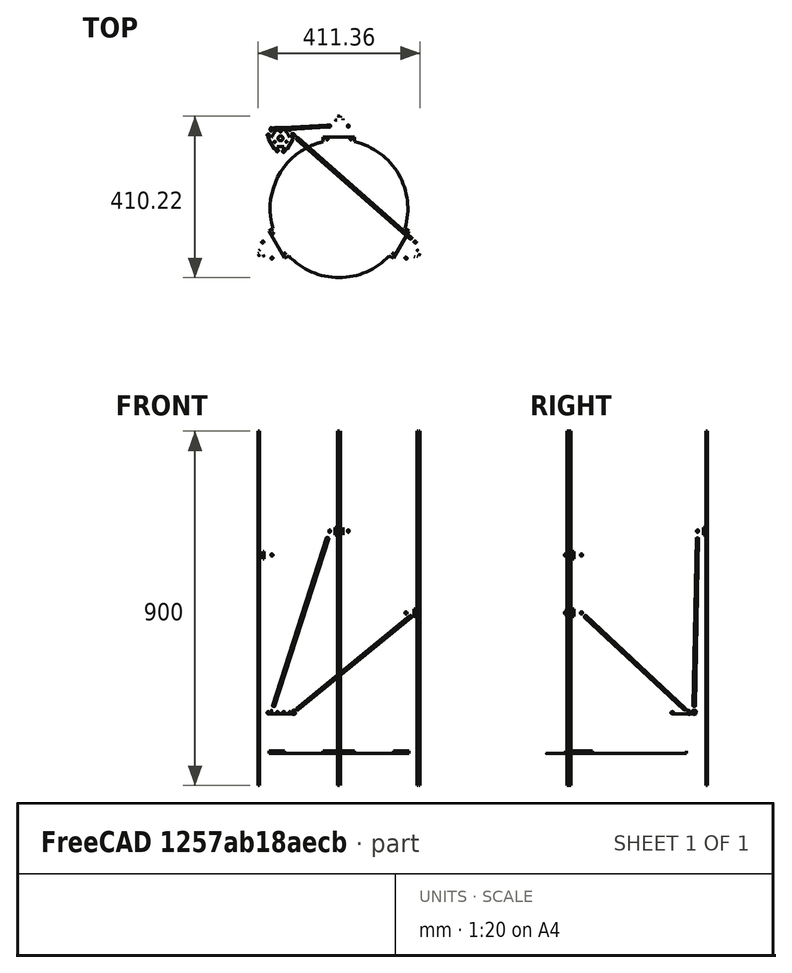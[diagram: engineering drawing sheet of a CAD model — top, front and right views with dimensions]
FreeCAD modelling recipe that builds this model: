
FCSTD DOCUMENT  (FreeCAD 2022.430R26244 +4758 (Git))
Label: AGAsm3MonsterKosselVs
License: All rights reserved
LicenseURL: http://en.wikipedia.org/wiki/All_rights_reserved
objects: App::FeaturePython×78, Part::FeaturePython×52, App::LinkElement×7, App::Link×4
note: 51 computed .brp shape members not serialized (recipe doc carries the construction recipe); baked Part::Feature solids carry a one-line shape summary decoded from their .brp
EXTERNAL_REF file=SubAs3Bati.FCStd obj=Assembly
EXTERNAL_REF file=SubAs3kossel_carriage_MGN9C.FCStd obj=Assembly
EXTERNAL_REF file=As3rod.FCStd obj=Assembly001
EXTERNAL_REF file=As3DeltaEffector.FCStd obj=Assembly002

FEATURE [App::Link] Link  label="SubAs3Bati"
  AutoLinkLabel = false
  AutoPlacement = true
  LinkedObject = -> <external SubAs3Bati.FCStd>#Assembly
  SyncGroupVisibility = false
  TreeRank = 0
  _LinkOwner = 275
  _LinkVersion = 1
FEATURE [App::LinkElement] Link001_i0
  LinkPlacement = pos=(163.421,1.55193e-09,3.43782) rot=(0,0,1;0rad)
  LinkedObject = -> <external SubAs3kossel_carriage_MGN9C.FCStd>#Assembly
  Placement = pos=(163.421,1.55193e-09,3.43782) rot=(0,0,1;0rad)
  TreeRank = 0
  _LinkOwner = 277
  _LinkVersion = 1
FEATURE [App::LinkElement] Link001_i1
  LinkPlacement = pos=(-44.3214,-201.973,353.265) rot=(1,0,0;4.18879rad)
  LinkedObject = -> <external SubAs3kossel_carriage_MGN9C.FCStd>#Assembly
  Placement = pos=(-44.3214,-201.973,353.265) rot=(1,0,0;4.18879rad)
  TreeRank = 0
  _LinkOwner = 277
  _LinkVersion = 1
FEATURE [App::LinkElement] Link001_i2
  LinkPlacement = pos=(16.3978,201.973,353.265) rot=(1,0,0;2.0944rad)
  LinkedObject = -> <external SubAs3kossel_carriage_MGN9C.FCStd>#Assembly
  Placement = pos=(16.3978,201.973,353.265) rot=(1,0,0;2.0944rad)
  TreeRank = 0
  _LinkOwner = 277
  _LinkVersion = 1
FEATURE [App::Link] Link001  label="SubAs3kossel_carriage_MGN9C"
  AutoLinkLabel = false
  AutoPlacement = true
  ElementCount = 3
  ElementList = -> [Link001_i0,Link001_i1,Link001_i2]
  LinkPlacement = pos=(204.95,-118.328,535) rot=(-0.694747,0.186157,0.694747;2.77349rad)
  LinkedObject = -> <external SubAs3kossel_carriage_MGN9C.FCStd>#Assembly
  Placement = pos=(204.95,-118.328,535) rot=(-0.694747,0.186157,0.694747;2.77349rad)
  SyncGroupVisibility = false
  TreeRank = 0
  _LinkOwner = 275
  _LinkVersion = 1
FEATURE [App::LinkElement] Link002_i0
  LinkPlacement = pos=(-35.9157,116.302,169.62) rot=(-0.350458,-0.806618,0.475969;5.10642rad)
  LinkedObject = -> <external As3rod.FCStd>#Assembly001
  Placement = pos=(-35.9157,116.302,169.62) rot=(-0.350458,-0.806618,0.475969;5.10642rad)
  TreeRank = 0
  _LinkOwner = 339
  _LinkVersion = 1
FEATURE [App::LinkElement] Link002_i1
  LinkPlacement = pos=(-133.494,204.013,223.964) rot=(-0.162867,0.145143,-0.975914;1.59805rad)
  LinkedObject = -> <external As3rod.FCStd>#Assembly001
  Placement = pos=(-133.494,204.013,223.964) rot=(-0.162867,0.145143,-0.975914;1.59805rad)
  TreeRank = 0
  _LinkOwner = 339
  _LinkVersion = 1
FEATURE [App::LinkElement] Link002_i2
  LinkPlacement = pos=(-160.329,76.1826,208.178) rot=(-0.107213,-0.289287,0.951219;3.72729rad)
  LinkedObject = -> <external As3rod.FCStd>#Assembly001
  Placement = pos=(-160.329,76.1826,208.178) rot=(-0.107213,-0.289287,0.951219;3.72729rad)
  TreeRank = 0
  _LinkOwner = 339
  _LinkVersion = 1
FEATURE [App::Link] Link003  label="As3DeltaEffector"
  AutoLinkLabel = false
  AutoPlacement = true
  LinkPlacement = pos=(-152.152,159.446,131.794) rot=(0,0,-1;3.66519rad)
  LinkedObject = -> <external As3DeltaEffector.FCStd>#Assembly002
  Placement = pos=(-152.152,159.446,131.794) rot=(0,0,-1;3.66519rad)
  SyncGroupVisibility = false
  TreeRank = 0
  _LinkOwner = 275
  _LinkVersion = 1
FEATURE [App::LinkElement] Link002_i3
  LinkPlacement = pos=(-59.4057,75.6158,169.62) rot=(-0.350454,-0.806617,0.475973;5.10642rad)
  LinkedObject = -> <external As3rod.FCStd>#Assembly001
  Placement = pos=(-59.4057,75.6158,169.62) rot=(-0.350454,-0.806617,0.475973;5.10642rad)
  TreeRank = 0
  _LinkOwner = 339
  _LinkVersion = 1
FEATURE [App::Link] Link002  label="As3Rod"
  AutoLinkLabel = false
  AutoPlacement = true
  ElementCount = 4
  ElementList = -> [Link002_i0,Link002_i1,Link002_i2,Link002_i3]
  LinkedObject = -> <external As3rod.FCStd>#Assembly001
  SyncGroupVisibility = false
  TreeRank = 0
  _LinkOwner = 275
  _LinkVersion = 1
FEATURE [Part::FeaturePython] Parts  # WARN: FeaturePython — macro-defined, semantics opaque (R4)
  Group = -> [Link,Link001,Link003,Link002]
  GroupMode = 0
  TreeRank = 0
  _LinkVersion = 1
FEATURE [Part::FeaturePython] Assembly  label="Asm3MonsterKossel"  # WARN: FeaturePython — macro-defined, semantics opaque (R4)
  AutoRelax = true
  BuildShape = 0
  Freeze = false
  Group = -> [Constraints,Elements,Parts]
  TreeRank = 0
  Verbose = false
  _LinkVersion = 1
  _SolverType = 1
  _Version = 1
FEATURE [App::FeaturePython] Constraints  # WARN: FeaturePython — macro-defined, semantics opaque (R4)
  Group = -> [Constraint,Constraint003,Constraint004,Constraint005,Constraint006,Constraint007,Constraint008,Constraint021,Constraint010,Constraint019,Constraint011,Constraint016,Constraint012,Constraint020,Constraint022,Constraint009,Constraint026,Constraint027,Constraint028,Constraint029,Constraint030,Constraint031,Constraint032,Constraint023,Constraint024,Constraint025]
  TreeRank = 0
  _LinkVersion = 1
  _Version = 1
FEATURE [App::FeaturePython] Elements  # WARN: FeaturePython — macro-defined, semantics opaque (R4)
  Group = -> [_Element,_Element002,_Element003,_Element005,_Element007,_Element008,_Element010,_Element013,_Element014,_Element015,_Element016,_Element017,_Element018,_Element019,_Element020,_Element021,_Element022,_Element023,_Element024,_Element025,_Element026,_Element027,_Element028,_Element030,_Element032,_Element034,_Element035,_Element036,_Element037,_Element038,_Element039,_Element040,_Element041,+17 more]
  TreeRank = 0
  _LinkVersion = 1
FEATURE [Part::FeaturePython] _Element  label="Fix@SubAs3Bati@#0"  # link proxy (typed FeaturePython)
  Detach = false
  LinkTransform = true
  LinkedObject = -> Link [1.$Fix@SubAs3Column@#0.]
  TreeRank = 0
  _LinkVersion = 1
  _Parent = -> Elements
FEATURE [App::FeaturePython] Constraint  label="Locked"  # WARN: FeaturePython — macro-defined, semantics opaque (R4)
  Disabled = false
  Group = -> [ElementLink]
  TreeRank = 0
  _ConstraintType = 0
  _LinkVersion = 1
  _Parent = -> Constraints
FEATURE [App::FeaturePython] ElementLink  label="Fix1@SubAs3Bati@"  # link proxy (typed FeaturePython)
  LinkTransform = true
  LinkedObject = -> _Element002
  TreeRank = 0
  _LinkVersion = 1
  _Parent = -> Constraint
FEATURE [Part::FeaturePython] _Element002  label="Fix1@SubAs3Bati@"  # link proxy (typed FeaturePython)
  Detach = false
  LinkTransform = true
  LinkedObject = -> Link [1.$Fix1@As3bed@.]
  TreeRank = 0
  _LinkVersion = 1
  _Parent = -> Elements
FEATURE [App::FeaturePython] Constraint003  label="PlaneAlignment"  # WARN: FeaturePython — macro-defined, semantics opaque (R4)
  Angle = 0
  AnglePitch = 0
  AngleRoll = 0
  Cascade = false
  Disabled = false
  Group = -> [ElementLink005,ElementLink006]
  LockAngle = false
  Offset = -10
  TreeRank = 0
  _ConstraintType = 37
  _LinkVersion = 1
  _Parent = -> Constraints
FEATURE [App::FeaturePython] ElementLink005  label="Ref@SubAs3Bati@#0"  # link proxy (typed FeaturePython)
  LinkTransform = true
  LinkedObject = -> _Element003
  TreeRank = 0
  _LinkVersion = 1
  _Parent = -> Constraint003
FEATURE [Part::FeaturePython] _Element003  label="Ref@SubAs3Bati@#0"  # link proxy (typed FeaturePython)
  Detach = false
  LinkTransform = true
  LinkedObject = -> Link [1.$Ref@SubAs3Column@#0.]
  TreeRank = 0
  _LinkVersion = 1
  _Parent = -> Elements
FEATURE [App::FeaturePython] ElementLink006  label="Ref@SubAs3kossel_carriage_MGN9C@#0"  # link proxy (typed FeaturePython)
  LinkTransform = true
  LinkedObject = -> _Element014
  TreeRank = 0
  _LinkVersion = 1
  _Parent = -> Constraint003
FEATURE [App::FeaturePython] Constraint004  label="PlaneAlignment001"  # WARN: FeaturePython — macro-defined, semantics opaque (R4)
  Angle = 0
  AnglePitch = 0
  AngleRoll = 0
  Cascade = false
  Disabled = false
  Group = -> [ElementLink007,ElementLink008]
  LockAngle = false
  Offset = -5.5
  TreeRank = 0
  _ConstraintType = 37
  _LinkVersion = 1
  _Parent = -> Constraints
FEATURE [App::FeaturePython] ElementLink007  label="Lat@SubAs3kossel_carriage_MGN9C@#0"  # link proxy (typed FeaturePython)
  LinkTransform = true
  LinkedObject = -> _Element015
  TreeRank = 0
  _LinkVersion = 1
  _Parent = -> Constraint004
FEATURE [App::FeaturePython] ElementLink008  label="Lat@SubAs3Bati@#0"  # link proxy (typed FeaturePython)
  LinkTransform = true
  LinkedObject = -> _Element005
  TreeRank = 0
  _LinkVersion = 1
  _Parent = -> Constraint004
FEATURE [Part::FeaturePython] _Element005  label="Lat@SubAs3Bati@#0"  # link proxy (typed FeaturePython)
  Detach = false
  LinkTransform = true
  LinkedObject = -> Link [1.$Lat@SubAs3Column@#0.]
  TreeRank = 0
  _LinkVersion = 1
  _Parent = -> Elements
FEATURE [App::FeaturePython] Constraint005  label="PlaneAlignment002"  # WARN: FeaturePython — macro-defined, semantics opaque (R4)
  Angle = 0
  AnglePitch = 0
  AngleRoll = 0
  Cascade = false
  Disabled = false
  Group = -> [ElementLink009,ElementLink010]
  LockAngle = false
  Offset = -10
  TreeRank = 0
  _ConstraintType = 37
  _LinkVersion = 1
  _Parent = -> Constraints
FEATURE [App::FeaturePython] ElementLink009  label="Ref@SubAs3kossel_carriage_MGN9C@#1"  # link proxy (typed FeaturePython)
  LinkTransform = true
  LinkedObject = -> _Element016
  TreeRank = 0
  _LinkVersion = 1
  _Parent = -> Constraint005
FEATURE [App::FeaturePython] ElementLink010  label="Ref@SubAs3Bati@#1"  # link proxy (typed FeaturePython)
  LinkTransform = true
  LinkedObject = -> _Element007
  TreeRank = 0
  _LinkVersion = 1
  _Parent = -> Constraint005
FEATURE [Part::FeaturePython] _Element007  label="Ref@SubAs3Bati@#1"  # link proxy (typed FeaturePython)
  Detach = false
  LinkTransform = true
  LinkedObject = -> Link [1.$Ref@SubAs3Column@#1.]
  TreeRank = 0
  _LinkVersion = 1
  _Parent = -> Elements
FEATURE [App::FeaturePython] Constraint006  label="PlaneAlignment003"  # WARN: FeaturePython — macro-defined, semantics opaque (R4)
  Angle = 0
  AnglePitch = 0
  AngleRoll = 0
  Cascade = false
  Disabled = false
  Group = -> [ElementLink011,ElementLink012]
  LockAngle = false
  Offset = 5.5
  TreeRank = 0
  _ConstraintType = 37
  _LinkVersion = 1
  _Parent = -> Constraints
FEATURE [App::FeaturePython] ElementLink011  label="Lat@SubAs3Bati@#1"  # link proxy (typed FeaturePython)
  LinkTransform = true
  LinkedObject = -> _Element008
  TreeRank = 0
  _LinkVersion = 1
  _Parent = -> Constraint006
FEATURE [Part::FeaturePython] _Element008  label="Lat@SubAs3Bati@#1"  # link proxy (typed FeaturePython)
  Detach = false
  LinkTransform = true
  LinkedObject = -> Link [1.$Lat@SubAs3Column@#1.]
  TreeRank = 0
  _LinkVersion = 1
  _Parent = -> Elements
FEATURE [App::FeaturePython] ElementLink012  label="Lat@SubAs3kossel_carriage_MGN9C@#1"  # link proxy (typed FeaturePython)
  LinkTransform = true
  LinkedObject = -> _Element017
  TreeRank = 0
  _LinkVersion = 1
  _Parent = -> Constraint006
FEATURE [App::FeaturePython] Constraint007  label="PlaneAlignment004"  # WARN: FeaturePython — macro-defined, semantics opaque (R4)
  Angle = 0
  AnglePitch = 0
  AngleRoll = 0
  Cascade = false
  Disabled = false
  Group = -> [ElementLink013,ElementLink014]
  LockAngle = false
  Offset = -10
  TreeRank = 0
  _ConstraintType = 37
  _LinkVersion = 1
  _Parent = -> Constraints
FEATURE [App::FeaturePython] ElementLink013  label="Ref@SubAs3Bati@#2"  # link proxy (typed FeaturePython)
  LinkTransform = true
  LinkedObject = -> _Element010
  TreeRank = 0
  _LinkVersion = 1
  _Parent = -> Constraint007
FEATURE [Part::FeaturePython] _Element010  label="Ref@SubAs3Bati@#2"  # link proxy (typed FeaturePython)
  Detach = false
  LinkTransform = true
  LinkedObject = -> Link [1.$Ref@SubAs3Column@#2.]
  TreeRank = 0
  _LinkVersion = 1
  _Parent = -> Elements
FEATURE [App::FeaturePython] ElementLink014  label="Ref@SubAs3kossel_carriage_MGN9C@#2"  # link proxy (typed FeaturePython)
  LinkTransform = true
  LinkedObject = -> _Element018
  TreeRank = 0
  _LinkVersion = 1
  _Parent = -> Constraint007
FEATURE [App::FeaturePython] Constraint008  label="PlaneAlignment005"  # WARN: FeaturePython — macro-defined, semantics opaque (R4)
  Angle = 0
  AnglePitch = 0
  AngleRoll = 0
  Cascade = false
  Disabled = false
  Group = -> [ElementLink015,ElementLink016]
  LockAngle = false
  Offset = -5.5
  TreeRank = 0
  _ConstraintType = 37
  _LinkVersion = 1
  _Parent = -> Constraints
FEATURE [App::FeaturePython] ElementLink015  label="Lat@SubAs3kossel_carriage_MGN9C@#2"  # link proxy (typed FeaturePython)
  LinkTransform = true
  LinkedObject = -> _Element019
  TreeRank = 0
  _LinkVersion = 1
  _Parent = -> Constraint008
FEATURE [App::FeaturePython] ElementLink016  label="Lat@SubAs3Bati@#2"  # link proxy (typed FeaturePython)
  LinkTransform = true
  LinkedObject = -> _Element013
  TreeRank = 0
  _LinkVersion = 1
  _Parent = -> Constraint008
FEATURE [Part::FeaturePython] _Element013  label="Lat@SubAs3Bati@#2"  # link proxy (typed FeaturePython)
  Detach = false
  LinkTransform = true
  LinkedObject = -> Link [1.$Lat@SubAs3Column@#2.]
  TreeRank = 0
  _LinkVersion = 1
  _Parent = -> Elements
FEATURE [Part::FeaturePython] _Element014  label="Ref@SubAs3kossel_carriage_MGN9C@#0"  # link proxy (typed FeaturePython)
  Detach = false
  LinkTransform = true
  LinkedObject = -> Link001 [Link001_i0.1.$Ref@As3MGN9CZFC-HiwinCorporation-3D-10-31-2021@.]
  TreeRank = 0
  _LinkVersion = 1
  _Parent = -> Elements
FEATURE [Part::FeaturePython] _Element015  label="Lat@SubAs3kossel_carriage_MGN9C@#0"  # link proxy (typed FeaturePython)
  Detach = false
  LinkTransform = true
  LinkedObject = -> Link001 [Link001_i0.1.$Lat@As3MGN9CZFC-HiwinCorporation-3D-10-31-2021@.]
  TreeRank = 0
  _LinkVersion = 1
  _Parent = -> Elements
FEATURE [Part::FeaturePython] _Element016  label="Ref@SubAs3kossel_carriage_MGN9C@#1"  # link proxy (typed FeaturePython)
  Detach = false
  LinkTransform = true
  LinkedObject = -> Link001 [Link001_i1.1.$Ref@As3MGN9CZFC-HiwinCorporation-3D-10-31-2021@.]
  TreeRank = 0
  _LinkVersion = 1
  _Parent = -> Elements
FEATURE [Part::FeaturePython] _Element017  label="Lat@SubAs3kossel_carriage_MGN9C@#1"  # link proxy (typed FeaturePython)
  Detach = false
  LinkTransform = true
  LinkedObject = -> Link001 [Link001_i1.1.$Lat@As3MGN9CZFC-HiwinCorporation-3D-10-31-2021@.]
  TreeRank = 0
  _LinkVersion = 1
  _Parent = -> Elements
FEATURE [Part::FeaturePython] _Element018  label="Ref@SubAs3kossel_carriage_MGN9C@#2"  # link proxy (typed FeaturePython)
  Detach = false
  LinkTransform = true
  LinkedObject = -> Link001 [Link001_i2.1.$Ref@As3MGN9CZFC-HiwinCorporation-3D-10-31-2021@.]
  TreeRank = 0
  _LinkVersion = 1
  _Parent = -> Elements
FEATURE [Part::FeaturePython] _Element019  label="Lat@SubAs3kossel_carriage_MGN9C@#2"  # link proxy (typed FeaturePython)
  Detach = false
  LinkTransform = true
  LinkedObject = -> Link001 [Link001_i2.1.$Lat@As3MGN9CZFC-HiwinCorporation-3D-10-31-2021@.]
  TreeRank = 0
  _LinkVersion = 1
  _Parent = -> Elements
FEATURE [App::FeaturePython] Constraint009  label="PlaneAlignment006"  # WARN: FeaturePython — macro-defined, semantics opaque (R4)
  Angle = 0
  AnglePitch = 0
  AngleRoll = 0
  Cascade = false
  Disabled = false
  Group = -> [ElementLink017,ElementLink018]
  LockAngle = false
  Offset = 100
  TreeRank = 0
  _ConstraintType = 37
  _LinkVersion = 1
  _Parent = -> Constraints
FEATURE [App::FeaturePython] ElementLink017  label="Element001@As3DeltaEffector@"  # link proxy (typed FeaturePython)
  LinkTransform = true
  LinkedObject = -> _Element020
  TreeRank = 0
  _LinkVersion = 1
  _Parent = -> Constraint009
FEATURE [Part::FeaturePython] _Element020  label="Element001@As3DeltaEffector@"  # link proxy (typed FeaturePython)
  Detach = false
  LinkTransform = true
  LinkedObject = -> Link003 [1.$Element001.]
  TreeRank = 0
  _LinkVersion = 1
  _Parent = -> Elements
FEATURE [App::FeaturePython] ElementLink018  label="_Element021"  # link proxy (typed FeaturePython)
  LinkTransform = true
  LinkedObject = -> _Element021
  TreeRank = 0
  _LinkVersion = 1
  _Parent = -> Constraint009
FEATURE [Part::FeaturePython] _Element021  # link proxy (typed FeaturePython)
  Detach = false
  LinkTransform = true
  LinkedObject = -> Link [1.$Element007.]
  TreeRank = 0
  _LinkVersion = 1
  _Parent = -> Elements
FEATURE [App::FeaturePython] Constraint010  label="PointsCoincident"  # WARN: FeaturePython — macro-defined, semantics opaque (R4)
  Disabled = false
  Group = -> [ElementLink019,ElementLink020]
  TreeRank = 0
  _ConstraintType = 1
  _LinkVersion = 1
  _Parent = -> Constraints
FEATURE [App::FeaturePython] ElementLink019  label="ElSphereF@As3Rod@#0#0"  # link proxy (typed FeaturePython)
  LinkTransform = true
  LinkedObject = -> _Element022
  TreeRank = 0
  _LinkVersion = 1
  _Parent = -> Constraint010
FEATURE [Part::FeaturePython] _Element022  label="ElSphereF@As3Rod@#0#0"  # link proxy (typed FeaturePython)
  Detach = false
  LinkTransform = true
  LinkedObject = -> Link002 [Link002_i0.1.$ElSphereF@As3rodEnd5347@#0.]
  TreeRank = 0
  _LinkVersion = 1
  _Parent = -> Elements
FEATURE [App::FeaturePython] ElementLink020  label="ElSphereM@As3DeltaEffector@#0"  # link proxy (typed FeaturePython)
  LinkTransform = true
  LinkedObject = -> _Element023
  TreeRank = 0
  _LinkVersion = 1
  _Parent = -> Constraint010
FEATURE [Part::FeaturePython] _Element023  label="ElSphereM@As3DeltaEffector@#0"  # link proxy (typed FeaturePython)
  Detach = false
  LinkTransform = true
  LinkedObject = -> Link003 [1.$ElSphereM@As3Traxxas5347ball@#0.]
  TreeRank = 0
  _LinkVersion = 1
  _Parent = -> Elements
FEATURE [App::FeaturePython] Constraint011  label="PointsCoincident009"  # WARN: FeaturePython — macro-defined, semantics opaque (R4)
  Disabled = false
  Group = -> [ElementLink021,ElementLink022]
  TreeRank = 0
  _ConstraintType = 1
  _LinkVersion = 1
  _Parent = -> Constraints
FEATURE [App::FeaturePython] ElementLink021  label="ElSphereM@As3DeltaEffector@#4"  # link proxy (typed FeaturePython)
  LinkTransform = true
  LinkedObject = -> _Element030
  TreeRank = 0
  _LinkVersion = 1
  _Parent = -> Constraint011
FEATURE [Part::FeaturePython] _Element024  label="ElSphereM@As3DeltaEffector@#1"  # link proxy (typed FeaturePython)
  Detach = false
  LinkTransform = true
  LinkedObject = -> Link003 [1.$ElSphereM@As3Traxxas5347ball@#1.]
  TreeRank = 0
  _LinkVersion = 1
  _Parent = -> Elements
FEATURE [App::FeaturePython] ElementLink022  label="ElSphereF@As3Rod@#0#1"  # link proxy (typed FeaturePython)
  LinkTransform = true
  LinkedObject = -> _Element025
  TreeRank = 0
  _LinkVersion = 1
  _Parent = -> Constraint011
FEATURE [Part::FeaturePython] _Element025  label="ElSphereF@As3Rod@#0#1"  # link proxy (typed FeaturePython)
  Detach = false
  LinkTransform = true
  LinkedObject = -> Link002 [Link002_i1.1.$ElSphereF@As3rodEnd5347@#0.]
  TreeRank = 0
  _LinkVersion = 1
  _Parent = -> Elements
FEATURE [App::FeaturePython] Constraint012  label="PointsCoincident010"  # WARN: FeaturePython — macro-defined, semantics opaque (R4)
  Disabled = false
  Group = -> [ElementLink023,ElementLink024]
  TreeRank = 0
  _ConstraintType = 1
  _LinkVersion = 1
  _Parent = -> Constraints
FEATURE [App::FeaturePython] ElementLink023  label="ElSphereM@As3DeltaEffector@#2"  # link proxy (typed FeaturePython)
  LinkTransform = true
  LinkedObject = -> _Element026
  TreeRank = 0
  _LinkVersion = 1
  _Parent = -> Constraint012
FEATURE [Part::FeaturePython] _Element026  label="ElSphereM@As3DeltaEffector@#2"  # link proxy (typed FeaturePython)
  Detach = false
  LinkTransform = true
  LinkedObject = -> Link003 [1.$ElSphereM@As3Traxxas5347ball@#2.]
  TreeRank = 0
  _LinkVersion = 1
  _Parent = -> Elements
FEATURE [App::FeaturePython] ElementLink024  label="ElSphereF@As3Rod@#0#2"  # link proxy (typed FeaturePython)
  LinkTransform = true
  LinkedObject = -> _Element027
  TreeRank = 0
  _LinkVersion = 1
  _Parent = -> Constraint012
FEATURE [Part::FeaturePython] _Element027  label="ElSphereF@As3Rod@#0#2"  # link proxy (typed FeaturePython)
  Detach = false
  LinkTransform = true
  LinkedObject = -> Link002 [Link002_i2.1.$ElSphereF@As3rodEnd5347@#0.]
  TreeRank = 0
  _LinkVersion = 1
  _Parent = -> Elements
FEATURE [Part::FeaturePython] _Element028  label="ElSphereM@As3DeltaEffector@#3"  # link proxy (typed FeaturePython)
  Detach = false
  LinkTransform = true
  LinkedObject = -> Link003 [1.$ElSphereM@As3Traxxas5347ball@#3.]
  TreeRank = 0
  _LinkVersion = 1
  _Parent = -> Elements
FEATURE [Part::FeaturePython] _Element030  label="ElSphereM@As3DeltaEffector@#4"  # link proxy (typed FeaturePython)
  Detach = false
  LinkTransform = true
  LinkedObject = -> Link003 [1.$ElSphereM@As3Traxxas5347ball@#4.]
  TreeRank = 0
  _LinkVersion = 1
  _Parent = -> Elements
FEATURE [Part::FeaturePython] _Element032  label="ElSphereM@As3DeltaEffector@#5"  # link proxy (typed FeaturePython)
  Detach = false
  LinkTransform = true
  LinkedObject = -> Link003 [1.$ElSphereM@As3Traxxas5347ball@#5.]
  TreeRank = 0
  _LinkVersion = 1
  _Parent = -> Elements
FEATURE [App::FeaturePython] Constraint016  label="PointsCoincident014"  # WARN: FeaturePython — macro-defined, semantics opaque (R4)
  Disabled = false
  Group = -> [ElementLink031,ElementLink032]
  TreeRank = 0
  _ConstraintType = 1
  _LinkVersion = 1
  _Parent = -> Constraints
FEATURE [App::FeaturePython] ElementLink031  label="ElSphereM@SubAs3kossel_carriage_MGN9C@#1#1"  # link proxy (typed FeaturePython)
  LinkTransform = true
  LinkedObject = -> _Element050
  TreeRank = 0
  _LinkVersion = 1
  _Parent = -> Constraint016
FEATURE [Part::FeaturePython] _Element034  label="ElSphereM@SubAs3kossel_carriage_MGN9C@#0#0"  # link proxy (typed FeaturePython)
  Detach = false
  LinkTransform = true
  LinkedObject = -> Link001 [Link001_i0.1.$ElSphereM@As3Traxxas5347ball@#0.]
  TreeRank = 0
  _LinkVersion = 1
  _Parent = -> Elements
FEATURE [App::FeaturePython] ElementLink032  label="ElSphereF@As3Rod@#1#1"  # link proxy (typed FeaturePython)
  LinkTransform = true
  LinkedObject = -> _Element035
  TreeRank = 0
  _LinkVersion = 1
  _Parent = -> Constraint016
FEATURE [Part::FeaturePython] _Element035  label="ElSphereF@As3Rod@#1#1"  # link proxy (typed FeaturePython)
  Detach = false
  LinkTransform = true
  LinkedObject = -> Link002 [Link002_i1.1.$ElSphereF@As3rodEnd5347@#1.]
  TreeRank = 0
  _LinkVersion = 1
  _Parent = -> Elements
FEATURE [Part::FeaturePython] _Element036  # link proxy (typed FeaturePython)
  Detach = false
  LinkTransform = true
  LinkedObject = -> Link002 [1.1.$Element004.]
  TreeRank = 0
  _LinkVersion = 1
  _Parent = -> Elements
FEATURE [Part::FeaturePython] _Element037  # link proxy (typed FeaturePython)
  Detach = false
  LinkTransform = true
  LinkedObject = -> Link003 [1.$Element011.]
  TreeRank = 0
  _LinkVersion = 1
  _Parent = -> Elements
FEATURE [Part::FeaturePython] _Element038  # link proxy (typed FeaturePython)
  Detach = false
  LinkTransform = true
  LinkedObject = -> Link003 [1.$Element012.]
  TreeRank = 0
  _LinkVersion = 1
  _Parent = -> Elements
FEATURE [Part::FeaturePython] _Element039  label="ElPlane@As3Rod@#001#0"  # link proxy (typed FeaturePython)
  Detach = false
  LinkTransform = true
  LinkedObject = -> Link002 [0.1.$ElPlane@As3rodEnd5347@#001.]
  TreeRank = 0
  _LinkVersion = 1
  _Parent = -> Elements
FEATURE [App::FeaturePython] Constraint019  label="PointsCoincident015"  # WARN: FeaturePython — macro-defined, semantics opaque (R4)
  Disabled = false
  Group = -> [ElementLink037,ElementLink038]
  TreeRank = 0
  _ConstraintType = 1
  _LinkVersion = 1
  _Parent = -> Constraints
FEATURE [App::FeaturePython] ElementLink037  label="ElSphereM@SubAs3kossel_carriage_MGN9C@#1#0"  # link proxy (typed FeaturePython)
  LinkTransform = true
  LinkedObject = -> _Element040
  TreeRank = 0
  _LinkVersion = 1
  _Parent = -> Constraint019
FEATURE [Part::FeaturePython] _Element040  label="ElSphereM@SubAs3kossel_carriage_MGN9C@#1#0"  # link proxy (typed FeaturePython)
  Detach = false
  LinkTransform = true
  LinkedObject = -> Link001 [Link001_i0.1.$ElSphereM@As3Traxxas5347ball@#1.]
  TreeRank = 0
  _LinkVersion = 1
  _Parent = -> Elements
FEATURE [App::FeaturePython] ElementLink038  label="ElSphereF@As3Rod@#1#0"  # link proxy (typed FeaturePython)
  LinkTransform = true
  LinkedObject = -> _Element041
  TreeRank = 0
  _LinkVersion = 1
  _Parent = -> Constraint019
FEATURE [Part::FeaturePython] _Element041  label="ElSphereF@As3Rod@#1#0"  # link proxy (typed FeaturePython)
  Detach = false
  LinkTransform = true
  LinkedObject = -> Link002 [Link002_i0.1.$ElSphereF@As3rodEnd5347@#1.]
  TreeRank = 0
  _LinkVersion = 1
  _Parent = -> Elements
FEATURE [App::FeaturePython] Constraint020  label="PointsCoincident008"  # WARN: FeaturePython — macro-defined, semantics opaque (R4)
  Disabled = false
  Group = -> [ElementLink039,ElementLink040]
  TreeRank = 0
  _ConstraintType = 1
  _LinkVersion = 1
  _Parent = -> Constraints
FEATURE [App::FeaturePython] ElementLink039  label="ElSphereM@SubAs3kossel_carriage_MGN9C@#1#2"  # link proxy (typed FeaturePython)
  LinkTransform = true
  LinkedObject = -> _Element042
  TreeRank = 0
  _LinkVersion = 1
  _Parent = -> Constraint020
FEATURE [Part::FeaturePython] _Element042  label="ElSphereM@SubAs3kossel_carriage_MGN9C@#1#2"  # link proxy (typed FeaturePython)
  Detach = false
  LinkTransform = true
  LinkedObject = -> Link001 [Link001_i2.1.$ElSphereM@As3Traxxas5347ball@#1.]
  TreeRank = 0
  _LinkVersion = 1
  _Parent = -> Elements
FEATURE [App::FeaturePython] ElementLink040  label="ElSphereF@As3Rod@#1#2"  # link proxy (typed FeaturePython)
  LinkTransform = true
  LinkedObject = -> _Element043
  TreeRank = 0
  _LinkVersion = 1
  _Parent = -> Constraint020
FEATURE [Part::FeaturePython] _Element043  label="ElSphereF@As3Rod@#1#2"  # link proxy (typed FeaturePython)
  Detach = false
  LinkTransform = true
  LinkedObject = -> Link002 [Link002_i2.1.$ElSphereF@As3rodEnd5347@#1.]
  TreeRank = 0
  _LinkVersion = 1
  _Parent = -> Elements
FEATURE [App::FeaturePython] Constraint021  label="Locked001"  # WARN: FeaturePython — macro-defined, semantics opaque (R4)
  Disabled = true
  Group = -> [ElementLink041]
  TreeRank = 0
  _ConstraintType = 0
  _LinkVersion = 1
  _Parent = -> Constraints
FEATURE [App::FeaturePython] ElementLink041  label="Element001@As3DeltaEffector@"  # link proxy (typed FeaturePython)
  LinkTransform = true
  LinkedObject = -> _Element020
  TreeRank = 0
  _LinkVersion = 1
  _Parent = -> Constraint021
FEATURE [Part::FeaturePython] _Element044  # link proxy (typed FeaturePython)
  Detach = false
  LinkTransform = true
  LinkedObject = -> Link002 [0.1.$Element007.]
  TreeRank = 0
  _LinkVersion = 1
  _Parent = -> Elements
FEATURE [Part::FeaturePython] _Element045  # link proxy (typed FeaturePython)
  Detach = false
  LinkTransform = true
  LinkedObject = -> Link002 [1.1.$Element007.]
  TreeRank = 0
  _LinkVersion = 1
  _Parent = -> Elements
FEATURE [Part::FeaturePython] _Element046  label="ElSphereM@SubAs3kossel_carriage_MGN9C@#0#2"  # link proxy (typed FeaturePython)
  Detach = false
  LinkTransform = true
  LinkedObject = -> Link001 [Link001_i2.1.$ElSphereM@As3Traxxas5347ball@#0.]
  TreeRank = 0
  _LinkVersion = 1
  _Parent = -> Elements
FEATURE [Part::FeaturePython] _Element048  label="ElSphereM@SubAs3kossel_carriage_MGN9C@#0#1"  # link proxy (typed FeaturePython)
  Detach = false
  LinkTransform = true
  LinkedObject = -> Link001 [Link001_i1.1.$ElSphereM@As3Traxxas5347ball@#0.]
  TreeRank = 0
  _LinkVersion = 1
  _Parent = -> Elements
FEATURE [Part::FeaturePython] _Element050  label="ElSphereM@SubAs3kossel_carriage_MGN9C@#1#1"  # link proxy (typed FeaturePython)
  Detach = false
  LinkTransform = true
  LinkedObject = -> Link001 [Link001_i1.1.$ElSphereM@As3Traxxas5347ball@#1.]
  TreeRank = 0
  _LinkVersion = 1
  _Parent = -> Elements
FEATURE [App::FeaturePython] Constraint022  label="PointsPlaneDistance"  # WARN: FeaturePython — macro-defined, semantics opaque (R4)
  Disabled = true
  Distance = 100
  Group = -> [ElementLink042,ElementLink043]
  TreeRank = 0
  _ConstraintType = 7
  _LinkVersion = 1
  _Parent = -> Constraints
FEATURE [App::FeaturePython] ElementLink042  label="_Element051"  # link proxy (typed FeaturePython)
  LinkTransform = true
  LinkedObject = -> _Element051
  TreeRank = 0
  _LinkVersion = 1
  _Parent = -> Constraint022
FEATURE [Part::FeaturePython] _Element051  # link proxy (typed FeaturePython)
  Detach = false
  LinkTransform = true
  LinkedObject = -> Link003 [1.$Element013.]
  TreeRank = 0
  _LinkVersion = 1
  _Parent = -> Elements
FEATURE [App::FeaturePython] ElementLink043  label="_Element021"  # link proxy (typed FeaturePython)
  LinkTransform = true
  LinkedObject = -> _Element021
  TreeRank = 0
  _LinkVersion = 1
  _Parent = -> Constraint022
FEATURE [App::FeaturePython] Constraint023  label="PointsPlaneDistance001"  # WARN: FeaturePython — macro-defined, semantics opaque (R4)
  Disabled = true
  Distance = -190
  Group = -> [ElementLink044,ElementLink045]
  TreeRank = 0
  _ConstraintType = 7
  _LinkVersion = 1
  _Parent = -> Constraints
FEATURE [App::FeaturePython] ElementLink044  label="_Element051"  # link proxy (typed FeaturePython)
  LinkTransform = true
  LinkedObject = -> _Element051
  TreeRank = 0
  _LinkVersion = 1
  _Parent = -> Constraint023
FEATURE [App::FeaturePython] ElementLink045  label="_Element052"  # link proxy (typed FeaturePython)
  LinkTransform = true
  LinkedObject = -> _Element052
  TreeRank = 0
  _LinkVersion = 1
  _Parent = -> Constraint023
FEATURE [Part::FeaturePython] _Element052  # link proxy (typed FeaturePython)
  Detach = false
  LinkTransform = true
  LinkedObject = -> Link [1.$Element008.]
  TreeRank = 0
  _LinkVersion = 1
  _Parent = -> Elements
FEATURE [App::FeaturePython] Constraint024  label="PointsPlaneDistance002"  # WARN: FeaturePython — macro-defined, semantics opaque (R4)
  Disabled = true
  Distance = -175
  Group = -> [ElementLink046,ElementLink047]
  TreeRank = 0
  _ConstraintType = 7
  _LinkVersion = 1
  _Parent = -> Constraints
FEATURE [App::FeaturePython] ElementLink046  label="_Element051"  # link proxy (typed FeaturePython)
  LinkTransform = true
  LinkedObject = -> _Element051
  TreeRank = 0
  _LinkVersion = 1
  _Parent = -> Constraint024
FEATURE [App::FeaturePython] ElementLink047  label="_Element053"  # link proxy (typed FeaturePython)
  LinkTransform = true
  LinkedObject = -> _Element053
  TreeRank = 0
  _LinkVersion = 1
  _Parent = -> Constraint024
FEATURE [Part::FeaturePython] _Element053  # link proxy (typed FeaturePython)
  Detach = false
  LinkTransform = true
  LinkedObject = -> Link [1.$Element009.]
  TreeRank = 0
  _LinkVersion = 1
  _Parent = -> Elements
FEATURE [App::FeaturePython] Constraint025  label="PointsPlaneDistance003"  # WARN: FeaturePython — macro-defined, semantics opaque (R4)
  Disabled = true
  Distance = -181.17
  Group = -> [ElementLink048,ElementLink049]
  TreeRank = 0
  _ConstraintType = 7
  _LinkVersion = 1
  _Parent = -> Constraints
FEATURE [App::FeaturePython] ElementLink048  label="_Element051"  # link proxy (typed FeaturePython)
  LinkTransform = true
  LinkedObject = -> _Element051
  TreeRank = 0
  _LinkVersion = 1
  _Parent = -> Constraint025
FEATURE [App::FeaturePython] ElementLink049  label="_Element054"  # link proxy (typed FeaturePython)
  LinkTransform = true
  LinkedObject = -> _Element054
  TreeRank = 0
  _LinkVersion = 1
  _Parent = -> Constraint025
FEATURE [Part::FeaturePython] _Element054  # link proxy (typed FeaturePython)
  Detach = false
  LinkTransform = true
  LinkedObject = -> Link [1.$Element010.]
  TreeRank = 0
  _LinkVersion = 1
  _Parent = -> Elements
FEATURE [App::FeaturePython] Constraint026  label="PointsCoincident016"  # WARN: FeaturePython — macro-defined, semantics opaque (R4)
  Disabled = false
  Group = -> [ElementLink050,ElementLink051]
  TreeRank = 0
  _ConstraintType = 1
  _LinkVersion = 1
  _Parent = -> Constraints
FEATURE [App::FeaturePython] ElementLink050  label="ElSphereM@As3DeltaEffector@#1"  # link proxy (typed FeaturePython)
  LinkTransform = true
  LinkedObject = -> _Element024
  TreeRank = 0
  _LinkVersion = 1
  _Parent = -> Constraint026
FEATURE [App::FeaturePython] ElementLink051  label="ElSphereF@As3Rod@#0#3"  # link proxy (typed FeaturePython)
  LinkTransform = true
  LinkedObject = -> _Element055
  TreeRank = 0
  _LinkVersion = 1
  _Parent = -> Constraint026
FEATURE [Part::FeaturePython] _Element055  label="ElSphereF@As3Rod@#0#3"  # link proxy (typed FeaturePython)
  Detach = false
  LinkTransform = true
  LinkedObject = -> Link002 [Link002_i3.1.$ElSphereF@As3rodEnd5347@#0.]
  TreeRank = 0
  _LinkVersion = 1
  _Parent = -> Elements
FEATURE [App::FeaturePython] Constraint027  label="PointsDistance"  # WARN: FeaturePython — macro-defined, semantics opaque (R4)
  Cascade = false
  Disabled = true
  Distance = 0.44
  Group = -> [ElementLink052,ElementLink053]
  TreeRank = 0
  _ConstraintType = 44
  _LinkVersion = 1
  _Parent = -> Constraints
FEATURE [App::FeaturePython] ElementLink052  label="ElSphereM@SubAs3kossel_carriage_MGN9C@#0#0"  # link proxy (typed FeaturePython)
  LinkTransform = true
  LinkedObject = -> _Element034
  TreeRank = 0
  _LinkVersion = 1
  _Parent = -> Constraint027
FEATURE [App::FeaturePython] ElementLink053  label="ElSphereF@As3Rod@#1#3"  # link proxy (typed FeaturePython)
  LinkTransform = true
  LinkedObject = -> _Element056
  TreeRank = 0
  _LinkVersion = 1
  _Parent = -> Constraint027
FEATURE [Part::FeaturePython] _Element056  label="ElSphereF@As3Rod@#1#3"  # link proxy (typed FeaturePython)
  Detach = false
  LinkTransform = true
  LinkedObject = -> Link002 [Link002_i3.1.$ElSphereF@As3rodEnd5347@#1.]
  TreeRank = 0
  _LinkVersion = 1
  _Parent = -> Elements
FEATURE [App::FeaturePython] Constraint028  label="PointsCoincident017"  # WARN: FeaturePython — macro-defined, semantics opaque (R4)
  Disabled = false
  Group = -> [ElementLink054,ElementLink055]
  TreeRank = 0
  _ConstraintType = 1
  _LinkVersion = 1
  _Parent = -> Constraints
FEATURE [App::FeaturePython] ElementLink054  label="ElSphereM@SubAs3kossel_carriage_MGN9C@#0#0"  # link proxy (typed FeaturePython)
  LinkTransform = true
  LinkedObject = -> _Element034
  TreeRank = 0
  _LinkVersion = 1
  _Parent = -> Constraint028
FEATURE [App::FeaturePython] ElementLink055  label="ElSphereF@As3Rod@#1#3"  # link proxy (typed FeaturePython)
  LinkTransform = true
  LinkedObject = -> _Element056
  TreeRank = 0
  _LinkVersion = 1
  _Parent = -> Constraint028
FEATURE [App::FeaturePython] Constraint029  label="PointInPlane"  # WARN: FeaturePython — macro-defined, semantics opaque (R4)
  Disabled = false
  Group = -> [ElementLink056,ElementLink057]
  TreeRank = 0
  _ConstraintType = 3
  _LinkVersion = 1
  _Parent = -> Constraints
FEATURE [App::FeaturePython] ElementLink056  label="ElSphereM@As3DeltaEffector@#1"  # link proxy (typed FeaturePython)
  LinkTransform = true
  LinkedObject = -> _Element024
  TreeRank = 0
  _LinkVersion = 1
  _Parent = -> Constraint029
FEATURE [App::FeaturePython] ElementLink057  label="ElSymSphF@As3Rod@#0#0"  # link proxy (typed FeaturePython)
  LinkTransform = true
  LinkedObject = -> _Element057
  TreeRank = 0
  _LinkVersion = 1
  _Parent = -> Constraint029
FEATURE [Part::FeaturePython] _Element057  label="ElSymSphF@As3Rod@#0#0"  # link proxy (typed FeaturePython)
  Detach = false
  LinkTransform = true
  LinkedObject = -> Link002 [Link002_i0.1.$ElSymSphF@As3rodEnd5347@#0.]
  TreeRank = 0
  _LinkVersion = 1
  _Parent = -> Elements
FEATURE [App::FeaturePython] Constraint030  label="PointInPlane001"  # WARN: FeaturePython — macro-defined, semantics opaque (R4)
  Disabled = false
  Group = -> [ElementLink058,ElementLink059]
  TreeRank = 0
  _ConstraintType = 3
  _LinkVersion = 1
  _Parent = -> Constraints
FEATURE [App::FeaturePython] ElementLink058  label="ElSphereM@As3DeltaEffector@#0"  # link proxy (typed FeaturePython)
  LinkTransform = true
  LinkedObject = -> _Element023
  TreeRank = 0
  _LinkVersion = 1
  _Parent = -> Constraint030
FEATURE [App::FeaturePython] ElementLink059  label="ElSymSphF@As3Rod@#0#3"  # link proxy (typed FeaturePython)
  LinkTransform = true
  LinkedObject = -> _Element058
  TreeRank = 0
  _LinkVersion = 1
  _Parent = -> Constraint030
FEATURE [Part::FeaturePython] _Element058  label="ElSymSphF@As3Rod@#0#3"  # link proxy (typed FeaturePython)
  Detach = false
  LinkTransform = true
  LinkedObject = -> Link002 [Link002_i3.1.$ElSymSphF@As3rodEnd5347@#0.]
  TreeRank = 0
  _LinkVersion = 1
  _Parent = -> Elements
FEATURE [App::FeaturePython] Constraint031  label="PointInPlane002"  # WARN: FeaturePython — macro-defined, semantics opaque (R4)
  Disabled = false
  Group = -> [ElementLink060,ElementLink061]
  TreeRank = 0
  _ConstraintType = 3
  _LinkVersion = 1
  _Parent = -> Constraints
FEATURE [App::FeaturePython] ElementLink060  label="ElSphereM@As3DeltaEffector@#3"  # link proxy (typed FeaturePython)
  LinkTransform = true
  LinkedObject = -> _Element028
  TreeRank = 0
  _LinkVersion = 1
  _Parent = -> Constraint031
FEATURE [App::FeaturePython] ElementLink061  label="ElSymSphF@As3Rod@#0#2"  # link proxy (typed FeaturePython)
  LinkTransform = true
  LinkedObject = -> _Element059
  TreeRank = 0
  _LinkVersion = 1
  _Parent = -> Constraint031
FEATURE [Part::FeaturePython] _Element059  label="ElSymSphF@As3Rod@#0#2"  # link proxy (typed FeaturePython)
  Detach = false
  LinkTransform = true
  LinkedObject = -> Link002 [Link002_i2.1.$ElSymSphF@As3rodEnd5347@#0.]
  TreeRank = 0
  _LinkVersion = 1
  _Parent = -> Elements
FEATURE [App::FeaturePython] Constraint032  label="PointInPlane003"  # WARN: FeaturePython — macro-defined, semantics opaque (R4)
  Disabled = false
  Group = -> [ElementLink062,ElementLink063]
  TreeRank = 0
  _ConstraintType = 3
  _LinkVersion = 1
  _Parent = -> Constraints
FEATURE [App::FeaturePython] ElementLink062  label="ElSphereM@As3DeltaEffector@#5"  # link proxy (typed FeaturePython)
  LinkTransform = true
  LinkedObject = -> _Element032
  TreeRank = 0
  _LinkVersion = 1
  _Parent = -> Constraint032
FEATURE [App::FeaturePython] ElementLink063  label="ElSymSphF@As3Rod@#0#1"  # link proxy (typed FeaturePython)
  LinkTransform = true
  LinkedObject = -> _Element060
  TreeRank = 0
  _LinkVersion = 1
  _Parent = -> Constraint032
FEATURE [Part::FeaturePython] _Element060  label="ElSymSphF@As3Rod@#0#1"  # link proxy (typed FeaturePython)
  Detach = false
  LinkTransform = true
  LinkedObject = -> Link002 [Link002_i1.1.$ElSymSphF@As3rodEnd5347@#0.]
  TreeRank = 0
  _LinkVersion = 1
  _Parent = -> Elements

RESOLVED EXTERNAL PARTS (link-assembly join: the EXTERNAL_REF files above that resolve inside this repo's crawl, each included once):
---- part As3DeltaEffector.FCStd = doc fcstd_bb46bd2530a1 ----
FCSTD DOCUMENT  (FreeCAD 2022.430R26244 +4758 (Git))
Label: As3DeltaEffector
License: All rights reserved
LicenseURL: http://en.wikipedia.org/wiki/All_rights_reserved
objects: Part::FeaturePython×30, App::FeaturePython×27, Part::Feature×9, App::LinkElement×6, App::Part×3, App::Link×2
note: 37 computed .brp shape members not serialized (recipe doc carries the construction recipe); baked Part::Feature solids carry a one-line shape summary decoded from their .brp
EXTERNAL_REF file=As3Traxxas5347BallJoint.FCStd obj=Assembly

FEATURE [App::FeaturePython] Constraints001  # WARN: FeaturePython — macro-defined, semantics opaque (R4)
  TreeRank = 258
  _LinkVersion = 1
  _Version = 1
FEATURE [Part::Feature] Solid  label="e3d nozzle (0.4)"
  Placement = pos=(0,-4.25,4e-16) rot=(0,0,1;0rad)
  TreeRank = 195
  shape: bbox 8.083 x 12.5 x 7 mm, 31 faces (baked)
FEATURE [Part::Feature] Solid001  label="e3d heaterblock"
  Placement = pos=(-5.5,-1.25,6.9e-15) rot=(0,0,1;0rad)
  TreeRank = 196
  shape: bbox 20 x 11.5 x 16 mm, 45 faces (baked)
FEATURE [Part::Feature] Solid002  label="e3d heat break"
  Placement = pos=(0,5.25,4e-16) rot=(0,0,1;0rad)
  TreeRank = 197
  shape: bbox 7 x 21.9 x 7 mm, 23 faces (baked)
FEATURE [Part::Feature] Solid003  label="e3d heatsink"
  Placement = pos=(0,12.35,4e-16) rot=(0,1,0;0.209118rad)
  TreeRank = 198
  shape: bbox 22.3 x 42.7 x 22.3 mm, 92 faces (baked)
FEATURE [Part::Feature] Solid004  label="fan duct"
  Placement = pos=(6.82793,2.62156,26.4875) rot=(0,0,1;0rad)
  TreeRank = 199
  shape: bbox 55.54 x 30 x 38.08 mm, 106 faces (baked)
FEATURE [Part::Feature] Solid005  label="fan sub1"
  Placement = pos=(-0.402046,15.9429,23.9537) rot=(0,0,1;0rad)
  TreeRank = 200
  shape: bbox 30 x 30 x 10 mm, 57 faces (baked)
FEATURE [Part::Feature] Solid006  label="fan sub2"
  Placement = pos=(-0.402046,15.9429,33.9537) rot=(-0.381664,-0.841822,-0.381664;1.74214rad)
  TreeRank = 201
  shape: bbox 29.15 x 29.85 x 8.5 mm, 30 faces (baked)
FEATURE [App::Part] Part  label="fan"
  ClaimAllChildren = false
  ExportMode = 1
  Group = -> [Solid005,Solid006]
  Origin = -> Origin001
  Placement = pos=(15.7816,1.67867,26.8895) rot=(0,-1,0;1.5708rad)
  TreeRank = 203
  _ExportChildren = -> [Solid005,Solid006]
  _GroupVersion = 1
FEATURE [App::Part] Part001  label="fanduct"
  ClaimAllChildren = false
  ExportMode = 1
  Group = -> [Solid004,Part]
  Origin = -> Origin002
  Placement = pos=(6.82793,9.72844,26.4875) rot=(0,1,0;3.14159rad)
  TreeRank = 205
  _ExportChildren = -> [Solid004,Part]
  _GroupVersion = 1
FEATURE [App::Part] Part002  label="e3d v6"
  ClaimAllChildren = false
  ExportMode = 1
  Group = -> [Solid,Solid001,Solid002,Solid003,Part001]
  Origin = -> Origin003
  Placement = pos=(65.8913,-6.33526,94.8) rot=(1,0.000157,0.000157;1.5708rad)
  TreeRank = 207
  _ExportChildren = -> [Solid,Solid001,Solid002,Solid003,Part001]
  _GroupVersion = 1
FEATURE [Part::FeaturePython] Parts001  # WARN: FeaturePython — macro-defined, semantics opaque (R4)
  Group = -> [Part002]
  GroupMode = 0
  TreeRank = 260
  _LinkVersion = 1
FEATURE [App::Link] Link001  label="AsE3dv007"
  AutoLinkLabel = false
  AutoPlacement = true
  LinkPlacement = pos=(-59.0731,-28.6152,-171.944) rot=(0,0,1;0.246235rad)
  LinkedObject = -> Assembly001
  Placement = pos=(-59.0731,-28.6152,-171.944) rot=(0,0,1;0.246235rad)
  SyncGroupVisibility = false
  TreeRank = 0
  _LinkOwner = 965
  _LinkVersion = 1
FEATURE [Part::Feature] Part__Feature044  label="Delta Effector"
  Placement = pos=(-5.1086,-20.3772,-4.35843) rot=(0,0,1;1.13446rad)
  TreeRank = 0
  shape: bbox 58.07 x 64.17 x 8.5 mm, 53 faces (baked)
FEATURE [App::LinkElement] Link_i0
  LinkPlacement = pos=(-16.625,-42.188,-28.294) rot=(0,0,-1;1.5708rad)
  LinkedObject = -> <external As3Traxxas5347BallJoint.FCStd>#Assembly
  Placement = pos=(-16.625,-42.188,-28.294) rot=(0,0,-1;1.5708rad)
  TreeRank = 265
  _LinkOwner = 548
  _LinkVersion = 1
FEATURE [App::LinkElement] Link_i1
  LinkPlacement = pos=(-16.625,4.79197,-28.294) rot=(0,0,-1;4.71239rad)
  LinkedObject = -> <external As3Traxxas5347BallJoint.FCStd>#Assembly
  Placement = pos=(-16.625,4.79197,-28.294) rot=(0,0,-1;4.71239rad)
  TreeRank = 266
  _LinkOwner = 548
  _LinkVersion = 1
FEATURE [App::LinkElement] Link_i2
  LinkPlacement = pos=(-2.46794,12.9656,-28.294) rot=(0,0,-1;3.66519rad)
  LinkedObject = -> <external As3Traxxas5347BallJoint.FCStd>#Assembly
  Placement = pos=(-2.46794,12.9656,-28.294) rot=(0,0,-1;3.66519rad)
  TreeRank = 267
  _LinkOwner = 548
  _LinkVersion = 1
FEATURE [App::LinkElement] Link_i3
  LinkPlacement = pos=(38.2179,-10.5244,-28.294) rot=(0,0,-1;0.523599rad)
  LinkedObject = -> <external As3Traxxas5347BallJoint.FCStd>#Assembly
  Placement = pos=(38.2179,-10.5244,-28.294) rot=(0,0,-1;0.523599rad)
  TreeRank = 268
  _LinkOwner = 548
  _LinkVersion = 1
FEATURE [App::LinkElement] Link_i4
  LinkPlacement = pos=(38.2179,-26.8716,-28.294) rot=(0,0,1;0.523599rad)
  LinkedObject = -> <external As3Traxxas5347BallJoint.FCStd>#Assembly
  Placement = pos=(38.2179,-26.8716,-28.294) rot=(0,0,1;0.523599rad)
  TreeRank = 269
  _LinkOwner = 548
  _LinkVersion = 1
FEATURE [App::LinkElement] Link_i5
  LinkPlacement = pos=(-2.46794,-50.3616,-28.294) rot=(0,0,-1;2.61799rad)
  LinkedObject = -> <external As3Traxxas5347BallJoint.FCStd>#Assembly
  Placement = pos=(-2.46794,-50.3616,-28.294) rot=(0,0,-1;2.61799rad)
  TreeRank = 270
  _LinkOwner = 548
  _LinkVersion = 1
FEATURE [App::Link] Link  label="As3Traxxas5347ball"
  AutoLinkLabel = false
  AutoPlacement = true
  ElementCount = 6
  ElementList = -> [Link_i0,Link_i1,Link_i2,Link_i3,Link_i4,Link_i5]
  LinkedObject = -> <external As3Traxxas5347BallJoint.FCStd>#Assembly
  SyncGroupVisibility = false
  TreeRank = 264
  _LinkOwner = 534
  _LinkVersion = 1
FEATURE [Part::FeaturePython] Parts002  # WARN: FeaturePython — macro-defined, semantics opaque (R4)
  Group = -> [Part__Feature044,Link001,Link]
  GroupMode = 0
  TreeRank = 0
  _LinkVersion = 1
FEATURE [Part::Feature] Solid007  label="5347 ball"
  TreeRank = 285
  shape: bbox 6.98 x 5.77 x 5.77 mm, 10 faces (baked)
FEATURE [Part::FeaturePython] Assembly001  label="AsE3dv6"  # WARN: FeaturePython — macro-defined, semantics opaque (R4)
  AutoRelax = true
  BuildShape = 0
  Freeze = true
  Group = -> [Constraints001,Elements001,Parts001]
  TreeRank = 261
  Verbose = false
  _LinkVersion = 1
  _SolverType = 1
  _Version = 1
FEATURE [App::FeaturePython] Elements001  # WARN: FeaturePython — macro-defined, semantics opaque (R4)
  Group = -> [Element005]
  TreeRank = 259
  _LinkVersion = 1
FEATURE [Part::FeaturePython] Assembly002  label="As3DeltaEffector"  # WARN: FeaturePython — macro-defined, semantics opaque (R4)
  AutoRelax = true
  BuildShape = 0
  Freeze = true
  Group = -> [Constraints002,Elements002,Parts002]
  TreeRank = 263
  Verbose = false
  _LinkVersion = 1
  _SolverType = 1
  _Version = 1
FEATURE [App::FeaturePython] Constraint  label="Locked"  # WARN: FeaturePython — macro-defined, semantics opaque (R4)
  Disabled = false
  Group = -> [ElementLink]
  TreeRank = 0
  _ConstraintType = 0
  _LinkVersion = 1
  _Parent = -> Constraints002
FEATURE [App::FeaturePython] Constraint001  label="PlaneCoincident"  # WARN: FeaturePython — macro-defined, semantics opaque (R4)
  Angle = 0
  AnglePitch = 0
  AngleRoll = 0
  Cascade = false
  Disabled = false
  Group = -> [ElementLink001,ElementLink002]
  LockAngle = false
  Multiply = false
  OffsetX = 0
  OffsetY = 0
  TreeRank = 0
  _ConstraintType = 35
  _LinkVersion = 1
  _Parent = -> Constraints002
FEATURE [App::FeaturePython] Constraint002  label="PlaneCoincident001"  # WARN: FeaturePython — macro-defined, semantics opaque (R4)
  Angle = 0
  AnglePitch = 0
  AngleRoll = 0
  Cascade = false
  Disabled = false
  Group = -> [ElementLink003,ElementLink004]
  LockAngle = false
  Multiply = false
  OffsetX = 0
  OffsetY = 0
  TreeRank = 0
  _ConstraintType = 35
  _LinkVersion = 1
  _Parent = -> Constraints002
FEATURE [App::FeaturePython] Constraint003  label="PlaneCoincident002"  # WARN: FeaturePython — macro-defined, semantics opaque (R4)
  Angle = 0
  AnglePitch = 0
  AngleRoll = 0
  Cascade = false
  Disabled = false
  Group = -> [ElementLink005,ElementLink006]
  LockAngle = false
  Multiply = false
  OffsetX = 0
  OffsetY = 0
  TreeRank = 0
  _ConstraintType = 35
  _LinkVersion = 1
  _Parent = -> Constraints002
FEATURE [App::FeaturePython] Constraint004  label="PlaneCoincident003"  # WARN: FeaturePython — macro-defined, semantics opaque (R4)
  Angle = 0
  AnglePitch = 0
  AngleRoll = 0
  Cascade = false
  Disabled = false
  Group = -> [ElementLink007,ElementLink008]
  LockAngle = false
  Multiply = false
  OffsetX = 0
  OffsetY = 0
  TreeRank = 0
  _ConstraintType = 35
  _LinkVersion = 1
  _Parent = -> Constraints002
FEATURE [App::FeaturePython] Constraint005  label="PlaneCoincident004"  # WARN: FeaturePython — macro-defined, semantics opaque (R4)
  Angle = 0
  AnglePitch = 0
  AngleRoll = 0
  Cascade = false
  Disabled = false
  Group = -> [ElementLink009,ElementLink010]
  LockAngle = false
  Multiply = false
  OffsetX = 0
  OffsetY = 0
  TreeRank = 0
  _ConstraintType = 35
  _LinkVersion = 1
  _Parent = -> Constraints002
FEATURE [App::FeaturePython] Constraint006  label="PlaneCoincident005"  # WARN: FeaturePython — macro-defined, semantics opaque (R4)
  Angle = 0
  AnglePitch = 0
  AngleRoll = 0
  Cascade = false
  Disabled = false
  Group = -> [ElementLink011,ElementLink012]
  LockAngle = false
  Multiply = false
  OffsetX = 0
  OffsetY = 0
  TreeRank = 0
  _ConstraintType = 35
  _LinkVersion = 1
  _Parent = -> Constraints002
FEATURE [App::FeaturePython] Constraints002  # WARN: FeaturePython — macro-defined, semantics opaque (R4)
  Group = -> [Constraint,Constraint001,Constraint002,Constraint003,Constraint004,Constraint005,Constraint006,Constraint007]
  TreeRank = 0
  _LinkVersion = 1
  _Version = 1
FEATURE [Part::FeaturePython] Element  label="ElSphereM@As3Traxxas5347ball@#3"  # link proxy (typed FeaturePython)
  Detach = false
  LinkTransform = true
  LinkedObject = -> Link [Link_i3.1.$ElSphereM.]
  TreeRank = 0
  _LinkVersion = 1
  _Parent = -> Elements002
FEATURE [Part::FeaturePython] Element004  label="Element001"  # link proxy (typed FeaturePython)
  Detach = false
  LinkTransform = true
  LinkedObject = -> Part__Feature044 [Face51]
  TreeRank = 0
  _LinkVersion = 1
  _Parent = -> Elements002
FEATURE [App::FeaturePython] ElementLink  label="_Element"  # link proxy (typed FeaturePython)
  LinkTransform = true
  LinkedObject = -> _Element
  TreeRank = 0
  _LinkVersion = 1
  _Parent = -> Constraint
FEATURE [App::FeaturePython] ElementLink001  label="ElCircle@As3Traxxas5347ball@#0"  # link proxy (typed FeaturePython)
  LinkTransform = true
  LinkedObject = -> _Element001
  TreeRank = 0
  _LinkVersion = 1
  _Parent = -> Constraint001
FEATURE [App::FeaturePython] ElementLink002  label="_Element002"  # link proxy (typed FeaturePython)
  LinkTransform = true
  LinkedObject = -> _Element002
  TreeRank = 0
  _LinkVersion = 1
  _Parent = -> Constraint001
FEATURE [App::FeaturePython] ElementLink003  label="ElCircle@As3Traxxas5347ball@#1"  # link proxy (typed FeaturePython)
  LinkTransform = true
  LinkedObject = -> _Element003
  TreeRank = 0
  _LinkVersion = 1
  _Parent = -> Constraint002
FEATURE [App::FeaturePython] ElementLink004  label="_Element004"  # link proxy (typed FeaturePython)
  LinkTransform = true
  LinkedObject = -> _Element004
  TreeRank = 0
  _LinkVersion = 1
  _Parent = -> Constraint002
FEATURE [App::FeaturePython] ElementLink005  label="ElCircle@As3Traxxas5347ball@#2"  # link proxy (typed FeaturePython)
  LinkTransform = true
  LinkedObject = -> _Element005
  TreeRank = 0
  _LinkVersion = 1
  _Parent = -> Constraint003
FEATURE [App::FeaturePython] ElementLink006  label="_Element006"  # link proxy (typed FeaturePython)
  LinkTransform = true
  LinkedObject = -> _Element006
  TreeRank = 0
  _LinkVersion = 1
  _Parent = -> Constraint003
FEATURE [App::FeaturePython] ElementLink007  label="ElCircle@As3Traxxas5347ball@#3"  # link proxy (typed FeaturePython)
  LinkTransform = true
  LinkedObject = -> _Element007
  TreeRank = 0
  _LinkVersion = 1
  _Parent = -> Constraint004
FEATURE [App::FeaturePython] ElementLink008  label="_Element008"  # link proxy (typed FeaturePython)
  LinkTransform = true
  LinkedObject = -> _Element008
  TreeRank = 0
  _LinkVersion = 1
  _Parent = -> Constraint004
FEATURE [App::FeaturePython] ElementLink009  label="ElCircle@As3Traxxas5347ball@#4"  # link proxy (typed FeaturePython)
  LinkTransform = true
  LinkedObject = -> _Element009
  TreeRank = 0
  _LinkVersion = 1
  _Parent = -> Constraint005
FEATURE [App::FeaturePython] ElementLink010  label="_Element010"  # link proxy (typed FeaturePython)
  LinkTransform = true
  LinkedObject = -> _Element010
  TreeRank = 0
  _LinkVersion = 1
  _Parent = -> Constraint005
FEATURE [App::FeaturePython] ElementLink011  label="ElCircle@As3Traxxas5347ball@#5"  # link proxy (typed FeaturePython)
  LinkTransform = true
  LinkedObject = -> _Element011
  TreeRank = 0
  _LinkVersion = 1
  _Parent = -> Constraint006
FEATURE [App::FeaturePython] ElementLink012  label="_Element012"  # link proxy (typed FeaturePython)
  LinkTransform = true
  LinkedObject = -> _Element012
  TreeRank = 0
  _LinkVersion = 1
  _Parent = -> Constraint006
FEATURE [App::FeaturePython] Elements002  # WARN: FeaturePython — macro-defined, semantics opaque (R4)
  Group = -> [_Element,_Element001,_Element002,_Element003,_Element004,_Element005,_Element006,_Element007,_Element008,_Element009,_Element010,_Element011,_Element012,Element,Element004,_Element013,_Element014,Element006,Element007,Element008,Element009,Element010,Element011,Element012,Element013]
  TreeRank = 0
  _LinkVersion = 1
FEATURE [Part::FeaturePython] _Element  # link proxy (typed FeaturePython)
  Detach = false
  LinkTransform = true
  LinkedObject = -> Part__Feature044 [Face50]
  TreeRank = 0
  _LinkVersion = 1
  _Parent = -> Elements002
FEATURE [Part::FeaturePython] _Element001  label="ElCircle@As3Traxxas5347ball@#0"  # link proxy (typed FeaturePython)
  Detach = false
  LinkTransform = true
  LinkedObject = -> Link [Link_i0.1.$ElCircle.]
  TreeRank = 0
  _LinkVersion = 1
  _Parent = -> Elements002
FEATURE [Part::FeaturePython] _Element002  # link proxy (typed FeaturePython)
  Detach = false
  LinkTransform = true
  LinkedObject = -> Part__Feature044 [Edge45]
  TreeRank = 0
  _LinkVersion = 1
  _Parent = -> Elements002
FEATURE [Part::FeaturePython] _Element003  label="ElCircle@As3Traxxas5347ball@#1"  # link proxy (typed FeaturePython)
  Detach = false
  LinkTransform = true
  LinkedObject = -> Link [Link_i1.1.$ElCircle.]
  TreeRank = 0
  _LinkVersion = 1
  _Parent = -> Elements002
FEATURE [Part::FeaturePython] _Element004  # link proxy (typed FeaturePython)
  Detach = false
  LinkTransform = true
  LinkedObject = -> Part__Feature044 [Edge44]
  TreeRank = 0
  _LinkVersion = 1
  _Parent = -> Elements002
FEATURE [Part::FeaturePython] _Element005  label="ElCircle@As3Traxxas5347ball@#2"  # link proxy (typed FeaturePython)
  Detach = false
  LinkTransform = true
  LinkedObject = -> Link [Link_i2.1.$ElCircle.]
  TreeRank = 0
  _LinkVersion = 1
  _Parent = -> Elements002
FEATURE [Part::FeaturePython] _Element006  # link proxy (typed FeaturePython)
  Detach = false
  LinkTransform = true
  LinkedObject = -> Part__Feature044 [Edge37]
  TreeRank = 0
  _LinkVersion = 1
  _Parent = -> Elements002
FEATURE [Part::FeaturePython] _Element007  label="ElCircle@As3Traxxas5347ball@#3"  # link proxy (typed FeaturePython)
  Detach = false
  LinkTransform = true
  LinkedObject = -> Link [Link_i3.1.$ElCircle.]
  TreeRank = 0
  _LinkVersion = 1
  _Parent = -> Elements002
FEATURE [Part::FeaturePython] _Element008  # link proxy (typed FeaturePython)
  Detach = false
  LinkTransform = true
  LinkedObject = -> Part__Feature044 [Edge36]
  TreeRank = 0
  _LinkVersion = 1
  _Parent = -> Elements002
FEATURE [Part::FeaturePython] _Element009  label="ElCircle@As3Traxxas5347ball@#4"  # link proxy (typed FeaturePython)
  Detach = false
  LinkTransform = true
  LinkedObject = -> Link [Link_i4.1.$ElCircle.]
  TreeRank = 0
  _LinkVersion = 1
  _Parent = -> Elements002
FEATURE [Part::FeaturePython] _Element010  # link proxy (typed FeaturePython)
  Detach = false
  LinkTransform = true
  LinkedObject = -> Part__Feature044 [Edge24]
  TreeRank = 0
  _LinkVersion = 1
  _Parent = -> Elements002
FEATURE [Part::FeaturePython] _Element011  label="ElCircle@As3Traxxas5347ball@#5"  # link proxy (typed FeaturePython)
  Detach = false
  LinkTransform = true
  LinkedObject = -> Link [Link_i5.1.$ElCircle.]
  TreeRank = 0
  _LinkVersion = 1
  _Parent = -> Elements002
FEATURE [Part::FeaturePython] _Element012  # link proxy (typed FeaturePython)
  Detach = false
  LinkTransform = true
  LinkedObject = -> Part__Feature044 [Edge23]
  TreeRank = 0
  _LinkVersion = 1
  _Parent = -> Elements002
FEATURE [App::FeaturePython] Constraint007  label="PlaneCoincident006"  # WARN: FeaturePython — macro-defined, semantics opaque (R4)
  Angle = 0
  AnglePitch = 0
  AngleRoll = 0
  Cascade = false
  Disabled = false
  Group = -> [ElementLink013,ElementLink014]
  LockAngle = false
  Multiply = false
  OffsetX = 0
  OffsetY = 0
  TreeRank = 271
  _ConstraintType = 35
  _LinkVersion = 1
  _Parent = -> Constraints002
FEATURE [App::FeaturePython] ElementLink013  label="_Element013"  # link proxy (typed FeaturePython)
  LinkTransform = true
  LinkedObject = -> _Element013
  TreeRank = 272
  _LinkVersion = 1
  _Parent = -> Constraint007
FEATURE [Part::FeaturePython] _Element013  # link proxy (typed FeaturePython)
  Detach = false
  LinkTransform = true
  LinkedObject = -> Part__Feature044 [Edge136]
  TreeRank = 273
  _LinkVersion = 1
  _Parent = -> Elements002
FEATURE [App::FeaturePython] ElementLink014  label="_Element014"  # link proxy (typed FeaturePython)
  LinkTransform = true
  LinkedObject = -> _Element014
  TreeRank = 274
  _LinkVersion = 1
  _Parent = -> Constraint007
FEATURE [Part::FeaturePython] Element005  # link proxy (typed FeaturePython)
  Detach = false
  LinkTransform = true
  LinkedObject = -> Part002 [Solid003.Edge147]
  TreeRank = 275
  _LinkVersion = 1
  _Parent = -> Elements001
FEATURE [Part::FeaturePython] _Element014  # link proxy (typed FeaturePython)
  Detach = false
  LinkTransform = true
  LinkedObject = -> Link001 [1.$Element005.]
  TreeRank = 276
  _LinkVersion = 1
  _Parent = -> Elements002
FEATURE [Part::FeaturePython] Element006  label="ElSphereM@As3Traxxas5347ball@#0"  # link proxy (typed FeaturePython)
  Detach = false
  LinkTransform = true
  LinkedObject = -> Link [Link_i0.1.$ElSphereM.]
  TreeRank = 277
  _LinkVersion = 1
  _Parent = -> Elements002
FEATURE [Part::FeaturePython] Element007  label="ElSphereM@As3Traxxas5347ball@#1"  # link proxy (typed FeaturePython)
  Detach = false
  LinkTransform = true
  LinkedObject = -> Link [Link_i1.1.$ElSphereM.]
  TreeRank = 278
  _LinkVersion = 1
  _Parent = -> Elements002
FEATURE [Part::FeaturePython] Element008  label="ElSphereM@As3Traxxas5347ball@#2"  # link proxy (typed FeaturePython)
  Detach = false
  LinkTransform = true
  LinkedObject = -> Link [Link_i2.1.$ElSphereM.]
  TreeRank = 279
  _LinkVersion = 1
  _Parent = -> Elements002
FEATURE [Part::FeaturePython] Element009  label="ElSphereM@As3Traxxas5347ball@#4"  # link proxy (typed FeaturePython)
  Detach = false
  LinkTransform = true
  LinkedObject = -> Link [Link_i4.1.$ElSphereM.]
  TreeRank = 280
  _LinkVersion = 1
  _Parent = -> Elements002
FEATURE [Part::FeaturePython] Element010  label="ElSphereM@As3Traxxas5347ball@#5"  # link proxy (typed FeaturePython)
  Detach = false
  LinkTransform = true
  LinkedObject = -> Link [Link_i5.1.$ElSphereM.]
  TreeRank = 281
  _LinkVersion = 1
  _Parent = -> Elements002
FEATURE [Part::FeaturePython] Element011  # link proxy (typed FeaturePython)
  Detach = false
  LinkTransform = true
  LinkedObject = -> Link [1.1.$Element007.]
  TreeRank = 282
  _LinkVersion = 1
  _Parent = -> Elements002
FEATURE [Part::FeaturePython] Element012  # link proxy (typed FeaturePython)
  Detach = false
  LinkTransform = true
  LinkedObject = -> Link [0.1.$Element007.]
  TreeRank = 283
  _LinkVersion = 1
  _Parent = -> Elements002
FEATURE [Part::FeaturePython] Element013  # link proxy (typed FeaturePython)
  Detach = false
  LinkTransform = true
  LinkedObject = -> Part__Feature044 [Edge135]
  TreeRank = 284
  _LinkVersion = 1
  _Parent = -> Elements002
---- part As3rod.FCStd = doc fcstd_76169eff3f36 ----
FCSTD DOCUMENT  (FreeCAD 2022.430R26244 +4758 (Git))
Label: As3rod
Comment: # 2020-05-30 22:08:10: read from <userpath>/Downloads/5347 ball.ipt
License: All rights reserved
LicenseURL: http://en.wikipedia.org/wiki/All_rights_reserved
objects: Part::FeaturePython×21, App::FeaturePython×15, App::LinkElement×2, Sketcher::SketchObject×1, PartDesign::Pad×1, PartDesign::Body×1, App::Link×1
note: 24 computed .brp shape members not serialized (recipe doc carries the construction recipe); baked Part::Feature solids carry a one-line shape summary decoded from their .brp
EXTERNAL_REF file=As3Traxxas5347BallJoint.FCStd obj=Assembly001

FEATURE [Sketcher::SketchObject] Sketch
  FullyConstrained = true
  MapMode = 5
  Support = -> [XY_Plane]
  TreeRank = 0
  sketch-geometry (2):
    g0: Circle CenterX=0 CenterY=0 CenterZ=0 NormalX=0 NormalY=0 NormalZ=1 AngleXU=0 Radius=1.8
    g1: Circle CenterX=0 CenterY=0 CenterZ=0 NormalX=0 NormalY=0 NormalZ=1 AngleXU=0 Radius=3
  constraints (4):
    c: Radius(g0) = 1.8
    c: Coincident(g1,g0)
    c: Radius(g1) = 3
    c: Coincident(g-1,g0)
FEATURE [PartDesign::Pad] Pad
  AddSubType = 0
  AlongSketchNormal = false
  CheckUpToFaceLimits = true
  ClaimChildren = false
  Direction = (0,0,1)
  Fit = 0
  FitJoin = 0
  InnerFit = 0
  InnerFitJoin = 0
  InnerTaperAngle = 0
  InnerTaperAngleRev = 0
  Length = 450
  Length2 = 100
  NewSolid = false
  Profile = -> Sketch
  Suppress = false
  TreeRank = 97
  Type = 0
  _ProfileBasedVersion = 0
FEATURE [PartDesign::Body] Body  label="Rod_length"
  AutoGroupSolids = false
  ClaimAllChildren = false
  ExportMode = 0
  Group = -> [Sketch,Pad]
  Origin = -> Origin
  Placement = pos=(-0.00421036,0.65715,-109.079) rot=(1,0,0;0.002472rad)
  Tip = -> Pad
  TreeRank = 123
  _ExportChildren = -> [Pad]
  _GroupVersion = 1
FEATURE [App::FeaturePython] Constraints  # WARN: FeaturePython — macro-defined, semantics opaque (R4)
  TreeRank = 125
  _LinkVersion = 1
  _Version = 1
FEATURE [Part::FeaturePython] Parts  # WARN: FeaturePython — macro-defined, semantics opaque (R4)
  Group = -> [Body]
  GroupMode = 0
  TreeRank = 127
  _LinkVersion = 1
FEATURE [App::LinkElement] Link002_i0
  LinkPlacement = pos=(-0.00436801,11.7109,-125.873) rot=(-0.70491,0.709132,-0.015268;2.9844rad)
  LinkedObject = -> <external As3Traxxas5347BallJoint.FCStd>#Assembly001
  Placement = pos=(-0.00436801,11.7109,-125.873) rot=(-0.70491,0.709132,-0.015268;2.9844rad)
  TreeRank = 138
  _LinkOwner = 1847
  _LinkVersion = 1
FEATURE [App::LinkElement] Link002_i1
  LinkPlacement = pos=(-0.00436801,-31.7158,356.849) rot=(0.110357,0.021394,0.993662;1.58312rad)
  LinkedObject = -> <external As3Traxxas5347BallJoint.FCStd>#Assembly001
  Placement = pos=(-0.00436801,-31.7158,356.849) rot=(0.110357,0.021394,0.993662;1.58312rad)
  TreeRank = 139
  _LinkOwner = 1847
  _LinkVersion = 1
FEATURE [App::Link] Link002  label="As3rodEnd5347"
  AutoLinkLabel = false
  AutoPlacement = true
  ElementCount = 2
  ElementList = -> [Link002_i0,Link002_i1]
  LinkPlacement = pos=(0,0,0) rot=(-1,0,0;0.087266rad)
  LinkedObject = -> <external As3Traxxas5347BallJoint.FCStd>#Assembly001
  Placement = pos=(0,0,0) rot=(-1,0,0;0.087266rad)
  SyncGroupVisibility = false
  TreeRank = 135
  _LinkVersion = 1
FEATURE [Part::FeaturePython] Assembly  label="As3RodTige"  # WARN: FeaturePython — macro-defined, semantics opaque (R4)
  AutoRelax = true
  BuildShape = 0
  Freeze = false
  Group = -> [Constraints,Elements,Parts]
  TreeRank = 124
  Verbose = false
  _LinkVersion = 1
  _SolverType = 1
  _Version = 1
FEATURE [App::FeaturePython] Elements  # WARN: FeaturePython — macro-defined, semantics opaque (R4)
  Group = -> [Element,Element001,Element006]
  TreeRank = 126
  _LinkVersion = 1
FEATURE [Part::FeaturePython] Element  label="ElExtrem1"  # link proxy (typed FeaturePython)
  Detach = false
  LinkTransform = true
  LinkedObject = -> Body [Pad.Edge2]
  TreeRank = 128
  _LinkVersion = 1
  _Parent = -> Elements
FEATURE [Part::FeaturePython] Element001  label="ElExtrem2"  # link proxy (typed FeaturePython)
  Detach = false
  LinkTransform = true
  LinkedObject = -> Body [Pad.Edge3]
  TreeRank = 129
  _LinkVersion = 1
  _Parent = -> Elements
FEATURE [Part::FeaturePython] Assembly001  label="As3Rod"  # WARN: FeaturePython — macro-defined, semantics opaque (R4)
  AutoRelax = true
  BuildShape = 0
  Freeze = true
  Group = -> [Constraints001,Elements001,Parts001]
  Placement = pos=(155.766,-39.6429,83.5098) rot=(0.482791,-0.679488,-0.552458;0.934964rad)
  TreeRank = 140
  Verbose = false
  _LinkVersion = 1
  _SolverType = 1
  _Version = 1
FEATURE [App::FeaturePython] Constraints001  # WARN: FeaturePython — macro-defined, semantics opaque (R4)
  Group = -> [Constraint,Constraint001,Constraint002,Constraint003]
  TreeRank = 141
  _LinkVersion = 1
  _Version = 1
FEATURE [App::FeaturePython] Elements001  # WARN: FeaturePython — macro-defined, semantics opaque (R4)
  Group = -> [_Element,_Element001,_Element002,_Element003,_Element004,_Element005,_Element006,_Element007,Element002,Element003,Element004,Element005,Element007,Element008]
  TreeRank = 142
  _LinkVersion = 1
FEATURE [Part::FeaturePython] Parts001  # WARN: FeaturePython — macro-defined, semantics opaque (R4)
  Group = -> [Assembly,Link002]
  GroupMode = 0
  TreeRank = 143
  _LinkVersion = 1
FEATURE [App::FeaturePython] Constraint  label="Locked"  # WARN: FeaturePython — macro-defined, semantics opaque (R4)
  Disabled = false
  Group = -> [ElementLink]
  TreeRank = 144
  _ConstraintType = 0
  _LinkVersion = 1
  _Parent = -> Constraints001
FEATURE [App::FeaturePython] ElementLink  label="ElExtrem1@As3RodTige@"  # link proxy (typed FeaturePython)
  LinkTransform = true
  LinkedObject = -> _Element
  TreeRank = 145
  _LinkVersion = 1
  _Parent = -> Constraint
FEATURE [Part::FeaturePython] _Element  label="ElExtrem1@As3RodTige@"  # link proxy (typed FeaturePython)
  Detach = false
  LinkTransform = true
  LinkedObject = -> Assembly [1.$ElExtrem1.]
  TreeRank = 146
  _LinkVersion = 1
  _Parent = -> Elements001
FEATURE [App::FeaturePython] Constraint001  label="Attachment"  # WARN: FeaturePython — macro-defined, semantics opaque (R4)
  Cascade = false
  Disabled = false
  Group = -> [ElementLink001,ElementLink002]
  Multiply = false
  TreeRank = 147
  _ConstraintType = 45
  _LinkVersion = 1
  _Parent = -> Constraints001
FEATURE [App::FeaturePython] ElementLink001  label="ElExtrem1@As3RodTige@"  # link proxy (typed FeaturePython)
  LinkTransform = true
  LinkedObject = -> _Element
  TreeRank = 148
  _LinkVersion = 1
  _Parent = -> Constraint001
FEATURE [App::FeaturePython] ElementLink002  label="ElCircle1@As3rodEnd5347@#0"  # link proxy (typed FeaturePython)
  LinkTransform = true
  LinkedObject = -> _Element006
  Offset = pos=(0,0,0) rot=(1,0,0;3.14159rad)
  Placement = pos=(2.42e-14,1.3143,-218.159) rot=(1,0,0;3.14159rad)
  TreeRank = 149
  _LinkVersion = 1
  _Parent = -> Constraint001
FEATURE [Part::FeaturePython] _Element001  label="ElCircle2@As3rodEnd5347@#1"  # link proxy (typed FeaturePython)
  Detach = false
  LinkTransform = true
  LinkedObject = -> Link002 [Link002_i1.1.$ElCircle2.]
  TreeRank = 150
  _LinkVersion = 1
  _Parent = -> Elements001
FEATURE [App::FeaturePython] Constraint002  label="Attachment001"  # WARN: FeaturePython — macro-defined, semantics opaque (R4)
  Cascade = false
  Disabled = false
  Group = -> [ElementLink003,ElementLink004]
  Multiply = false
  TreeRank = 151
  _ConstraintType = 45
  _LinkVersion = 1
  _Parent = -> Constraints001
FEATURE [App::FeaturePython] ElementLink003  label="ElCircle1@As3rodEnd5347@#1"  # link proxy (typed FeaturePython)
  LinkTransform = true
  LinkedObject = -> _Element007
  TreeRank = 152
  _LinkVersion = 1
  _Parent = -> Constraint002
FEATURE [Part::FeaturePython] _Element002  label="ElCircle2@As3rodEnd5347@#0"  # link proxy (typed FeaturePython)
  Detach = false
  LinkTransform = true
  LinkedObject = -> Link002 [Link002_i0.1.$ElCircle2.]
  TreeRank = 153
  _LinkVersion = 1
  _Parent = -> Elements001
FEATURE [App::FeaturePython] ElementLink004  label="ElExtrem2@As3RodTige@"  # link proxy (typed FeaturePython)
  LinkTransform = true
  LinkedObject = -> _Element003
  TreeRank = 154
  _LinkVersion = 1
  _Parent = -> Constraint002
FEATURE [Part::FeaturePython] _Element003  label="ElExtrem2@As3RodTige@"  # link proxy (typed FeaturePython)
  Detach = false
  LinkTransform = true
  LinkedObject = -> Assembly [1.$ElExtrem2.]
  TreeRank = 155
  _LinkVersion = 1
  _Parent = -> Elements001
FEATURE [Part::FeaturePython] _Element004  label="ElPlane@As3rodEnd5347@#0"  # link proxy (typed FeaturePython)
  Detach = false
  LinkTransform = true
  LinkedObject = -> Link002 [Link002_i0.1.$ElPlane.]
  TreeRank = 158
  _LinkVersion = 1
  _Parent = -> Elements001
FEATURE [Part::FeaturePython] _Element005  label="ElPlane@As3rodEnd5347@#1"  # link proxy (typed FeaturePython)
  Detach = false
  LinkTransform = true
  LinkedObject = -> Link002 [Link002_i1.1.$ElPlane.]
  TreeRank = 160
  _LinkVersion = 1
  _Parent = -> Elements001
FEATURE [Part::FeaturePython] _Element006  label="ElCircle1@As3rodEnd5347@#0"  # link proxy (typed FeaturePython)
  Detach = false
  LinkTransform = true
  LinkedObject = -> Link002 [Link002_i0.1.$ElCircle1.]
  TreeRank = 161
  _LinkVersion = 1
  _Parent = -> Elements001
FEATURE [Part::FeaturePython] _Element007  label="ElCircle1@As3rodEnd5347@#1"  # link proxy (typed FeaturePython)
  Detach = false
  LinkTransform = true
  LinkedObject = -> Link002 [Link002_i1.1.$ElCircle1.]
  TreeRank = 162
  _LinkVersion = 1
  _Parent = -> Elements001
FEATURE [App::FeaturePython] Constraint003  label="SameOrientation"  # WARN: FeaturePython — macro-defined, semantics opaque (R4)
  Disabled = true
  Group = -> [ElementLink005,ElementLink006]
  TreeRank = 163
  _ConstraintType = 2
  _LinkVersion = 1
  _Parent = -> Constraints001
FEATURE [App::FeaturePython] ElementLink005  label="ElPlane@As3rodEnd5347@#0"  # link proxy (typed FeaturePython)
  LinkTransform = true
  LinkedObject = -> _Element004
  TreeRank = 164
  _LinkVersion = 1
  _Parent = -> Constraint003
FEATURE [App::FeaturePython] ElementLink006  label="ElPlane@As3rodEnd5347@#1"  # link proxy (typed FeaturePython)
  LinkTransform = true
  LinkedObject = -> _Element005
  TreeRank = 165
  _LinkVersion = 1
  _Parent = -> Constraint003
FEATURE [Part::FeaturePython] Element002  label="ElSphereF@As3rodEnd5347@#0"  # link proxy (typed FeaturePython)
  Detach = false
  LinkTransform = true
  LinkedObject = -> Link002 [Link002_i0.1.$ElSphereF.]
  TreeRank = 166
  _LinkVersion = 1
  _Parent = -> Elements001
FEATURE [Part::FeaturePython] Element003  label="ElSphereF@As3rodEnd5347@#1"  # link proxy (typed FeaturePython)
  Detach = false
  LinkTransform = true
  LinkedObject = -> Link002 [Link002_i1.1.$ElSphereF.]
  TreeRank = 167
  _LinkVersion = 1
  _Parent = -> Elements001
FEATURE [Part::FeaturePython] Element004  # link proxy (typed FeaturePython)
  Detach = false
  LinkTransform = true
  LinkedObject = -> Link002 [0.1.$Element006.]
  TreeRank = 168
  _LinkVersion = 1
  _Parent = -> Elements001
FEATURE [Part::FeaturePython] Element005  label="ElPlane@As3rodEnd5347@#001"  # link proxy (typed FeaturePython)
  Detach = false
  LinkTransform = true
  LinkedObject = -> Link002 [0.1.$ElPlane.]
  TreeRank = 169
  _LinkVersion = 1
  _Parent = -> Elements001
FEATURE [Part::FeaturePython] Element006  # link proxy (typed FeaturePython)
  Detach = false
  LinkTransform = true
  LinkedObject = -> Body [Pad.Face1]
  TreeRank = 170
  _LinkVersion = 1
  _Parent = -> Elements
FEATURE [Part::FeaturePython] Element007  # link proxy (typed FeaturePython)
  Detach = false
  LinkTransform = true
  LinkedObject = -> Assembly [1.$Element006.]
  TreeRank = 171
  _LinkVersion = 1
  _Parent = -> Elements001
FEATURE [Part::FeaturePython] Element008  label="ElSymSphF@As3rodEnd5347@#0"  # link proxy (typed FeaturePython)
  Detach = false
  LinkTransform = true
  LinkedObject = -> Link002 [Link002_i0.1.$ElSymSphF.]
  TreeRank = 172
  _LinkVersion = 1
  _Parent = -> Elements001
---- part SubAs3Bati.FCStd = doc fcstd_e7f4b90d9a3b ----
FCSTD DOCUMENT  (FreeCAD 2022.430R26244 +4758 (Git))
Label: SubAs3Bati
License: All rights reserved
LicenseURL: http://en.wikipedia.org/wiki/All_rights_reserved
objects: Part::FeaturePython×25, App::FeaturePython×22, App::LinkElement×3, App::Link×2
note: 24 computed .brp shape members not serialized (recipe doc carries the construction recipe); baked Part::Feature solids carry a one-line shape summary decoded from their .brp
EXTERNAL_REF file=SubAs3Column.FCStd obj=Assembly
EXTERNAL_REF file=As3bed.FCStd obj=Assembly

FEATURE [App::LinkElement] Link_i0
  LinkPlacement = pos=(263.894,-152.359,-81) rot=(0,0,1;1.0472rad)
  LinkedObject = -> <external SubAs3Column.FCStd>#Assembly
  Placement = pos=(263.894,-152.359,-81) rot=(0,0,1;1.0472rad)
  TreeRank = 0
  _LinkOwner = 4511
  _LinkVersion = 1
FEATURE [App::LinkElement] Link_i1
  LinkPlacement = pos=(-5.8111e-11,304.718,-81) rot=(0,0,1;3.14159rad)
  LinkedObject = -> <external SubAs3Column.FCStd>#Assembly
  Placement = pos=(-5.8111e-11,304.718,-81) rot=(0,0,1;3.14159rad)
  TreeRank = 0
  _LinkOwner = 4511
  _LinkVersion = 1
FEATURE [App::LinkElement] Link_i2
  LinkPlacement = pos=(-263.894,-152.359,-81) rot=(0,0,-1;1.0472rad)
  LinkedObject = -> <external SubAs3Column.FCStd>#Assembly
  Placement = pos=(-263.894,-152.359,-81) rot=(0,0,-1;1.0472rad)
  TreeRank = 0
  _LinkOwner = 4511
  _LinkVersion = 1
FEATURE [App::Link] Link  label="SubAs3Column"
  AutoLinkLabel = false
  AutoPlacement = true
  ElementCount = 3
  ElementList = -> [Link_i0,Link_i1,Link_i2]
  LinkedObject = -> <external SubAs3Column.FCStd>#Assembly
  SyncGroupVisibility = false
  TreeRank = 0
  _LinkOwner = 4510
  _LinkVersion = 1
FEATURE [App::Link] Link001  label="As3Bed"
  AutoLinkLabel = false
  AutoPlacement = true
  LinkedObject = -> <external As3bed.FCStd>#Assembly
  SyncGroupVisibility = false
  TreeRank = 0
  _LinkOwner = 4510
  _LinkVersion = 1
FEATURE [Part::FeaturePython] Parts  # WARN: FeaturePython — macro-defined, semantics opaque (R4)
  Group = -> [Link001,Link]
  GroupMode = 0
  TreeRank = 0
  _LinkVersion = 1
FEATURE [Part::FeaturePython] Assembly  label="SubAs3Bati"  # WARN: FeaturePython — macro-defined, semantics opaque (R4)
  AutoRelax = true
  BuildShape = 0
  Freeze = false
  Group = -> [Constraints,Elements,Parts]
  TreeRank = 0
  Verbose = false
  _LinkVersion = 1
  _SolverType = 1
  _Version = 1
FEATURE [App::FeaturePython] Constraints  # WARN: FeaturePython — macro-defined, semantics opaque (R4)
  Group = -> [Constraint,Constraint001,Constraint002,Constraint003,Constraint004,Constraint005,Constraint006]
  TreeRank = 0
  _LinkVersion = 1
  _Version = 1
FEATURE [App::FeaturePython] Elements  # WARN: FeaturePython — macro-defined, semantics opaque (R4)
  Group = -> [_Element,_Element001,_Element002,_Element003,_Element004,_Element005,_Element006,_Element007,_Element008,_Element009,_Element010,_Element011,Element,Element001,Element002,Element003,Element004,Element005,Element006,Element007,Element008,Element009,Element010]
  TreeRank = 0
  _LinkVersion = 1
FEATURE [App::FeaturePython] Constraint  label="Locked"  # WARN: FeaturePython — macro-defined, semantics opaque (R4)
  Disabled = false
  Group = -> [ElementLink]
  TreeRank = 0
  _ConstraintType = 0
  _LinkVersion = 1
  _Parent = -> Constraints
FEATURE [App::FeaturePython] ElementLink  label="Fix1@As3bed@"  # link proxy (typed FeaturePython)
  LinkTransform = true
  LinkedObject = -> _Element
  TreeRank = 0
  _LinkVersion = 1
  _Parent = -> Constraint
FEATURE [Part::FeaturePython] _Element  label="Fix1@As3bed@"  # link proxy (typed FeaturePython)
  Detach = false
  LinkTransform = true
  LinkedObject = -> Link001 [1.$Fix1.]
  TreeRank = 0
  _LinkVersion = 1
  _Parent = -> Elements
FEATURE [App::FeaturePython] Constraint001  label="PlaneCoincident"  # WARN: FeaturePython — macro-defined, semantics opaque (R4)
  Angle = 0
  AnglePitch = 0
  AngleRoll = 0
  Cascade = false
  Disabled = false
  Group = -> [ElementLink001,ElementLink002]
  LockAngle = false
  Multiply = false
  OffsetX = 0
  OffsetY = 0
  TreeRank = 0
  _ConstraintType = 35
  _LinkVersion = 1
  _Parent = -> Constraints
FEATURE [App::FeaturePython] ElementLink001  label="Fix1@As3bed@"  # link proxy (typed FeaturePython)
  LinkTransform = true
  LinkedObject = -> _Element
  TreeRank = 0
  _LinkVersion = 1
  _Parent = -> Constraint001
FEATURE [App::FeaturePython] ElementLink002  label="Fix3@SubAs3Column@#0"  # link proxy (typed FeaturePython)
  LinkTransform = true
  LinkedObject = -> _Element001
  TreeRank = 0
  _LinkVersion = 1
  _Parent = -> Constraint001
FEATURE [Part::FeaturePython] _Element001  label="Fix3@SubAs3Column@#0"  # link proxy (typed FeaturePython)
  Detach = false
  LinkTransform = true
  LinkedObject = -> Link [Link_i0.1.$Fix3@As3motorFrame@.]
  TreeRank = 0
  _LinkVersion = 1
  _Parent = -> Elements
FEATURE [App::FeaturePython] Constraint002  label="PlaneCoincident001"  # WARN: FeaturePython — macro-defined, semantics opaque (R4)
  Angle = 0
  AnglePitch = 0
  AngleRoll = 0
  Cascade = false
  Disabled = false
  Group = -> [ElementLink003,ElementLink004]
  LockAngle = false
  Multiply = false
  OffsetX = 0
  OffsetY = 0
  TreeRank = 0
  _ConstraintType = 35
  _LinkVersion = 1
  _Parent = -> Constraints
FEATURE [App::FeaturePython] ElementLink003  label="Fix2@As3bed@"  # link proxy (typed FeaturePython)
  LinkTransform = true
  LinkedObject = -> _Element002
  TreeRank = 0
  _LinkVersion = 1
  _Parent = -> Constraint002
FEATURE [Part::FeaturePython] _Element002  label="Fix2@As3bed@"  # link proxy (typed FeaturePython)
  Detach = false
  LinkTransform = true
  LinkedObject = -> Link001 [1.$Fix2.]
  TreeRank = 0
  _LinkVersion = 1
  _Parent = -> Elements
FEATURE [App::FeaturePython] ElementLink004  label="Fix4@SubAs3Column@#0"  # link proxy (typed FeaturePython)
  LinkTransform = true
  LinkedObject = -> _Element003
  TreeRank = 0
  _LinkVersion = 1
  _Parent = -> Constraint002
FEATURE [Part::FeaturePython] _Element003  label="Fix4@SubAs3Column@#0"  # link proxy (typed FeaturePython)
  Detach = false
  LinkTransform = true
  LinkedObject = -> Link [Link_i0.1.$Fix4@As3motorFrame@.]
  TreeRank = 0
  _LinkVersion = 1
  _Parent = -> Elements
FEATURE [App::FeaturePython] Constraint003  label="PlaneCoincident002"  # WARN: FeaturePython — macro-defined, semantics opaque (R4)
  Angle = 0
  AnglePitch = 0
  AngleRoll = 0
  Cascade = false
  Disabled = false
  Group = -> [ElementLink005,ElementLink006]
  LockAngle = false
  Multiply = false
  OffsetX = 0
  OffsetY = 0
  TreeRank = 0
  _ConstraintType = 35
  _LinkVersion = 1
  _Parent = -> Constraints
FEATURE [App::FeaturePython] ElementLink005  label="Fix3@SubAs3Column@#1"  # link proxy (typed FeaturePython)
  LinkTransform = true
  LinkedObject = -> _Element004
  TreeRank = 0
  _LinkVersion = 1
  _Parent = -> Constraint003
FEATURE [Part::FeaturePython] _Element004  label="Fix3@SubAs3Column@#1"  # link proxy (typed FeaturePython)
  Detach = false
  LinkTransform = true
  LinkedObject = -> Link [Link_i1.1.$Fix3@As3motorFrame@.]
  TreeRank = 0
  _LinkVersion = 1
  _Parent = -> Elements
FEATURE [App::FeaturePython] ElementLink006  label="Fix3@As3bed@"  # link proxy (typed FeaturePython)
  LinkTransform = true
  LinkedObject = -> _Element005
  TreeRank = 0
  _LinkVersion = 1
  _Parent = -> Constraint003
FEATURE [Part::FeaturePython] _Element005  label="Fix3@As3bed@"  # link proxy (typed FeaturePython)
  Detach = false
  LinkTransform = true
  LinkedObject = -> Link001 [1.$Fix3.]
  TreeRank = 0
  _LinkVersion = 1
  _Parent = -> Elements
FEATURE [App::FeaturePython] Constraint004  label="PlaneCoincident003"  # WARN: FeaturePython — macro-defined, semantics opaque (R4)
  Angle = 0
  AnglePitch = 0
  AngleRoll = 0
  Cascade = false
  Disabled = false
  Group = -> [ElementLink007,ElementLink008]
  LockAngle = false
  Multiply = false
  OffsetX = 0
  OffsetY = 0
  TreeRank = 0
  _ConstraintType = 35
  _LinkVersion = 1
  _Parent = -> Constraints
FEATURE [App::FeaturePython] ElementLink007  label="Fix4@SubAs3Column@#1"  # link proxy (typed FeaturePython)
  LinkTransform = true
  LinkedObject = -> _Element006
  TreeRank = 0
  _LinkVersion = 1
  _Parent = -> Constraint004
FEATURE [Part::FeaturePython] _Element006  label="Fix4@SubAs3Column@#1"  # link proxy (typed FeaturePython)
  Detach = false
  LinkTransform = true
  LinkedObject = -> Link [Link_i1.1.$Fix4@As3motorFrame@.]
  TreeRank = 0
  _LinkVersion = 1
  _Parent = -> Elements
FEATURE [App::FeaturePython] ElementLink008  label="Fix4@As3bed@"  # link proxy (typed FeaturePython)
  LinkTransform = true
  LinkedObject = -> _Element007
  TreeRank = 0
  _LinkVersion = 1
  _Parent = -> Constraint004
FEATURE [Part::FeaturePython] _Element007  label="Fix4@As3bed@"  # link proxy (typed FeaturePython)
  Detach = false
  LinkTransform = true
  LinkedObject = -> Link001 [1.$Fix4.]
  TreeRank = 0
  _LinkVersion = 1
  _Parent = -> Elements
FEATURE [App::FeaturePython] Constraint005  label="PlaneCoincident004"  # WARN: FeaturePython — macro-defined, semantics opaque (R4)
  Angle = 0
  AnglePitch = 0
  AngleRoll = 0
  Cascade = false
  Disabled = false
  Group = -> [ElementLink009,ElementLink010]
  LockAngle = false
  Multiply = false
  OffsetX = 0
  OffsetY = 0
  TreeRank = 0
  _ConstraintType = 35
  _LinkVersion = 1
  _Parent = -> Constraints
FEATURE [App::FeaturePython] ElementLink009  label="Fix3@SubAs3Column@#2"  # link proxy (typed FeaturePython)
  LinkTransform = true
  LinkedObject = -> _Element008
  TreeRank = 0
  _LinkVersion = 1
  _Parent = -> Constraint005
FEATURE [Part::FeaturePython] _Element008  label="Fix3@SubAs3Column@#2"  # link proxy (typed FeaturePython)
  Detach = false
  LinkTransform = true
  LinkedObject = -> Link [Link_i2.1.$Fix3@As3motorFrame@.]
  TreeRank = 0
  _LinkVersion = 1
  _Parent = -> Elements
FEATURE [App::FeaturePython] ElementLink010  label="Fix5@As3bed@"  # link proxy (typed FeaturePython)
  LinkTransform = true
  LinkedObject = -> _Element009
  TreeRank = 0
  _LinkVersion = 1
  _Parent = -> Constraint005
FEATURE [Part::FeaturePython] _Element009  label="Fix5@As3bed@"  # link proxy (typed FeaturePython)
  Detach = false
  LinkTransform = true
  LinkedObject = -> Link001 [1.$Fix5.]
  TreeRank = 0
  _LinkVersion = 1
  _Parent = -> Elements
FEATURE [App::FeaturePython] Constraint006  label="PlaneCoincident005"  # WARN: FeaturePython — macro-defined, semantics opaque (R4)
  Angle = 0
  AnglePitch = 0
  AngleRoll = 0
  Cascade = false
  Disabled = false
  Group = -> [ElementLink011,ElementLink012]
  LockAngle = false
  Multiply = false
  OffsetX = 0
  OffsetY = 0
  TreeRank = 0
  _ConstraintType = 35
  _LinkVersion = 1
  _Parent = -> Constraints
FEATURE [App::FeaturePython] ElementLink011  label="Fix4@SubAs3Column@#2"  # link proxy (typed FeaturePython)
  LinkTransform = true
  LinkedObject = -> _Element010
  TreeRank = 0
  _LinkVersion = 1
  _Parent = -> Constraint006
FEATURE [Part::FeaturePython] _Element010  label="Fix4@SubAs3Column@#2"  # link proxy (typed FeaturePython)
  Detach = false
  LinkTransform = true
  LinkedObject = -> Link [Link_i2.1.$Fix4@As3motorFrame@.]
  TreeRank = 0
  _LinkVersion = 1
  _Parent = -> Elements
FEATURE [App::FeaturePython] ElementLink012  label="Fix6@As3bed@"  # link proxy (typed FeaturePython)
  LinkTransform = true
  LinkedObject = -> _Element011
  TreeRank = 0
  _LinkVersion = 1
  _Parent = -> Constraint006
FEATURE [Part::FeaturePython] _Element011  label="Fix6@As3bed@"  # link proxy (typed FeaturePython)
  Detach = false
  LinkTransform = true
  LinkedObject = -> Link001 [1.$Fix6.]
  TreeRank = 0
  _LinkVersion = 1
  _Parent = -> Elements
FEATURE [Part::FeaturePython] Element  label="Fix@SubAs3Column@#0"  # link proxy (typed FeaturePython)
  Detach = false
  LinkTransform = true
  LinkedObject = -> Link [Link_i0.1.$Fix@As3MGNR9R900CM-HiwinCorporation-3D-10-31-2021@.]
  TreeRank = 0
  _LinkVersion = 1
  _Parent = -> Elements
FEATURE [Part::FeaturePython] Element001  label="Ref@SubAs3Column@#0"  # link proxy (typed FeaturePython)
  Detach = false
  LinkTransform = true
  LinkedObject = -> Link [Link_i0.1.$Ref@As3MGNR9R900CM-HiwinCorporation-3D-10-31-2021@.]
  TreeRank = 0
  _LinkVersion = 1
  _Parent = -> Elements
FEATURE [Part::FeaturePython] Element002  label="Lat@SubAs3Column@#0"  # link proxy (typed FeaturePython)
  Detach = false
  LinkTransform = true
  LinkedObject = -> Link [Link_i0.1.$Lat@As3MGNR9R900CM-HiwinCorporation-3D-10-31-2021@.]
  TreeRank = 0
  _LinkVersion = 1
  _Parent = -> Elements
FEATURE [Part::FeaturePython] Element003  label="Ref@SubAs3Column@#1"  # link proxy (typed FeaturePython)
  Detach = false
  LinkTransform = true
  LinkedObject = -> Link [Link_i1.1.$Ref@As3MGNR9R900CM-HiwinCorporation-3D-10-31-2021@.]
  TreeRank = 0
  _LinkVersion = 1
  _Parent = -> Elements
FEATURE [Part::FeaturePython] Element004  label="Lat@SubAs3Column@#1"  # link proxy (typed FeaturePython)
  Detach = false
  LinkTransform = true
  LinkedObject = -> Link [Link_i1.1.$Lat@As3MGNR9R900CM-HiwinCorporation-3D-10-31-2021@.]
  TreeRank = 0
  _LinkVersion = 1
  _Parent = -> Elements
FEATURE [Part::FeaturePython] Element005  label="Ref@SubAs3Column@#2"  # link proxy (typed FeaturePython)
  Detach = false
  LinkTransform = true
  LinkedObject = -> Link [Link_i2.1.$Ref@As3MGNR9R900CM-HiwinCorporation-3D-10-31-2021@.]
  TreeRank = 0
  _LinkVersion = 1
  _Parent = -> Elements
FEATURE [Part::FeaturePython] Element006  label="Lat@SubAs3Column@#2"  # link proxy (typed FeaturePython)
  Detach = false
  LinkTransform = true
  LinkedObject = -> Link [Link_i2.1.$Lat@As3MGNR9R900CM-HiwinCorporation-3D-10-31-2021@.]
  TreeRank = 0
  _LinkVersion = 1
  _Parent = -> Elements
FEATURE [Part::FeaturePython] Element007  # link proxy (typed FeaturePython)
  Detach = false
  LinkTransform = true
  LinkedObject = -> Link001 [1.$Element006.]
  TreeRank = 0
  _LinkVersion = 1
  _Parent = -> Elements
FEATURE [Part::FeaturePython] Element008  # link proxy (typed FeaturePython)
  Detach = false
  LinkTransform = true
  LinkedObject = -> Link001 [1.$Element007.]
  TreeRank = 0
  _LinkVersion = 1
  _Parent = -> Elements
FEATURE [Part::FeaturePython] Element009  # link proxy (typed FeaturePython)
  Detach = false
  LinkTransform = true
  LinkedObject = -> Link001 [1.$Element008.]
  TreeRank = 0
  _LinkVersion = 1
  _Parent = -> Elements
FEATURE [Part::FeaturePython] Element010  # link proxy (typed FeaturePython)
  Detach = false
  LinkTransform = true
  LinkedObject = -> Link001 [1.$Element009.]
  TreeRank = 0
  _LinkVersion = 1
  _Parent = -> Elements
---- part SubAs3kossel_carriage_MGN9C.FCStd = doc fcstd_a01fffbfabfb ----
FCSTD DOCUMENT  (FreeCAD 2022.430R26244 +4758 (Git))
Label: SubAs3kossel_carriage_MGN9C
License: All rights reserved
LicenseURL: http://en.wikipedia.org/wiki/All_rights_reserved
objects: Part::Feature×21, Part::FeaturePython×16, App::FeaturePython×16, App::Link×7, App::LinkGroup×2, App::DocumentObjectGroup×2, App::LinkElement×2
note: 36 computed .brp shape members not serialized (recipe doc carries the construction recipe); baked Part::Feature solids carry a one-line shape summary decoded from their .brp
EXTERNAL_REF file=as3MGN9CZFC-HiwinCorporation-3D-10-31-2021.FCStd obj=Assembly
EXTERNAL_REF file=as3carriage_MGN9C.FCStd obj=Assembly

FEATURE [App::Link] Link  label="As3MGN9CZFC-HiwinCorporation-3D-10-31-2021"
  AutoLinkLabel = false
  AutoPlacement = true
  LinkedObject = -> <external as3MGN9CZFC-HiwinCorporation-3D-10-31-2021.FCStd>#Assembly
  SyncGroupVisibility = false
  TreeRank = 0
  _LinkOwner = 4486
  _LinkVersion = 1
FEATURE [App::Link] Link001  label="As3carriage_MGN9C"
  AutoLinkLabel = false
  AutoPlacement = true
  LinkPlacement = pos=(14.45,2.4e-15,8) rot=(0,0,1;1.5708rad)
  LinkedObject = -> <external as3carriage_MGN9C.FCStd>#Assembly
  Placement = pos=(14.45,2.4e-15,8) rot=(0,0,1;1.5708rad)
  SyncGroupVisibility = false
  TreeRank = 0
  _LinkOwner = 4486
  _LinkVersion = 1
FEATURE [Part::Feature] Solid  label="PRODUCT_NAME_1"
  TreeRank = 11
  shape: bbox 18.9 x 20 x 8 mm, 90 faces (baked)
FEATURE [Part::Feature] Solid001  label="PRODUCT_NAME_2"
  TreeRank = 12
  shape: bbox 4 x 19.6 x 7.7 mm, 40 faces (baked)
FEATURE [Part::Feature] Solid002  label="PRODUCT_NAME_3"
  TreeRank = 13
  shape: bbox 4 x 19.6 x 7.7 mm, 40 faces (baked)
FEATURE [Part::Feature] Solid003  label="PRODUCT_NAME_4"
  TreeRank = 14
  shape: bbox 1 x 19.6 x 7.7 mm, 46 faces (baked)
FEATURE [Part::Feature] Solid004  label="PRODUCT_NAME_5"
  TreeRank = 15
  shape: bbox 1 x 19.6 x 7.7 mm, 46 faces (baked)
FEATURE [Part::Feature] Solid005  label="PRODUCT_NAME_6"
  TreeRank = 16
  shape: bbox 0.9 x 2 x 2 mm, 18 faces (baked)
FEATURE [Part::Feature] Solid006  label="PRODUCT_NAME_7"
  TreeRank = 17
  shape: bbox 0.9 x 2 x 2 mm, 18 faces (baked)
FEATURE [Part::Feature] Solid007  label="PRODUCT_NAME_8"
  TreeRank = 18
  shape: bbox 0.9 x 2 x 2 mm, 18 faces (baked)
FEATURE [Part::Feature] Solid008  label="PRODUCT_NAME_9"
  TreeRank = 19
  shape: bbox 0.9 x 2 x 2 mm, 18 faces (baked)
FEATURE [App::LinkGroup] LinkGroup
  ElementList = -> [Solid,Solid001,Solid002,Solid003,Solid004,Solid005,Solid006,Solid007,Solid008]
  LinkMode = 0
  TreeRank = 36
  _LinkVersion = 1
FEATURE [Part::Feature] Solid009  label="carriage_MGN9C"
  TreeRank = 37
  shape: bbox 40 x 30 x 21 mm, 75 faces (baked)
FEATURE [App::Link] Link004  label="Link004(As3MGN9CZFC-HiwinCorporation-3D-10-31-2021)"
  AutoLinkLabel = true
  AutoPlacement = true
  LinkedObject = -> Link
  SyncGroupVisibility = false
  TreeRank = 38
  _LinkVersion = 1
FEATURE [App::Link] Link005  label="Link005(As3carriage_MGN9C)"
  AutoLinkLabel = true
  AutoPlacement = true
  LinkPlacement = pos=(14.45,-2.64669e-11,8) rot=(0,0,1;1.5708rad)
  LinkedObject = -> Link001
  Placement = pos=(14.45,-2.64669e-11,8) rot=(0,0,1;1.5708rad)
  SyncGroupVisibility = false
  TreeRank = 39
  _LinkVersion = 1
FEATURE [Part::Feature] Solid010  label="PRODUCT_NAME_010"
  TreeRank = 11
  shape: bbox 18.9 x 20 x 8 mm, 90 faces (baked)
FEATURE [Part::Feature] Solid011  label="PRODUCT_NAME_011"
  TreeRank = 12
  shape: bbox 4 x 19.6 x 7.7 mm, 40 faces (baked)
FEATURE [Part::Feature] Solid012  label="PRODUCT_NAME_012"
  TreeRank = 13
  shape: bbox 4 x 19.6 x 7.7 mm, 40 faces (baked)
FEATURE [Part::Feature] Solid013  label="PRODUCT_NAME_013"
  TreeRank = 14
  shape: bbox 1 x 19.6 x 7.7 mm, 46 faces (baked)
FEATURE [Part::Feature] Solid014  label="PRODUCT_NAME_014"
  TreeRank = 15
  shape: bbox 1 x 19.6 x 7.7 mm, 46 faces (baked)
FEATURE [Part::Feature] Solid015  label="PRODUCT_NAME_015"
  TreeRank = 16
  shape: bbox 0.9 x 2 x 2 mm, 18 faces (baked)
FEATURE [Part::Feature] Solid016  label="PRODUCT_NAME_016"
  TreeRank = 17
  shape: bbox 0.9 x 2 x 2 mm, 18 faces (baked)
FEATURE [Part::Feature] Solid017  label="PRODUCT_NAME_017"
  TreeRank = 18
  shape: bbox 0.9 x 2 x 2 mm, 18 faces (baked)
FEATURE [Part::Feature] Solid018  label="PRODUCT_NAME_018"
  TreeRank = 19
  shape: bbox 0.9 x 2 x 2 mm, 18 faces (baked)
FEATURE [App::LinkGroup] LinkGroup001
  ElementList = -> [Solid010,Solid011,Solid012,Solid013,Solid014,Solid015,Solid016,Solid017,Solid018]
  LinkMode = 0
  TreeRank = 35
  _LinkVersion = 1
FEATURE [Part::Feature] Solid019  label="carriage_MGN9C001"
  TreeRank = 34
  shape: bbox 40 x 30 x 21 mm, 75 faces (baked)
FEATURE [App::Link] Link008  label="Link008(As3MGN9CZFC-HiwinCorporation-3D-10-31-2021)"
  AutoLinkLabel = true
  AutoPlacement = true
  LinkedObject = -> Link
  SyncGroupVisibility = false
  TreeRank = 32
  _LinkVersion = 1
FEATURE [App::Link] Link009  label="Link009(As3carriage_MGN9C)"
  AutoLinkLabel = true
  AutoPlacement = true
  LinkPlacement = pos=(14.45,-2.64669e-11,8) rot=(0,0,1;1.5708rad)
  LinkedObject = -> Link001
  Placement = pos=(14.45,-2.64669e-11,8) rot=(0,0,1;1.5708rad)
  SyncGroupVisibility = false
  TreeRank = 33
  _LinkVersion = 1
FEATURE [App::DocumentObjectGroup] Group  label="Groupe"
  ClaimAllChildren = true
  ExportMode = 1
  Group = -> [LinkGroup,Solid009,Link004,Link005]
  TreeRank = 40
  _GroupVersion = 1
FEATURE [App::DocumentObjectGroup] Group001  label="Groupe001"
  ClaimAllChildren = true
  ExportMode = 1
  Group = -> [Solid019,LinkGroup001,Link008,Link009]
  TreeRank = 41
  _GroupVersion = 1
FEATURE [App::LinkElement] Link010_i0
  LinkPlacement = pos=(14.45,23.49,23) rot=(0,0,1;1.5708rad)
  LinkedObject = -> Solid020
  Placement = pos=(14.45,23.49,23) rot=(0,0,1;1.5708rad)
  TreeRank = 46
  _LinkOwner = 4607
  _LinkVersion = 1
FEATURE [App::LinkElement] Link010_i1
  LinkPlacement = pos=(14.45,-23.49,23) rot=(0,0,-1;1.5708rad)
  LinkedObject = -> Solid020
  Placement = pos=(14.45,-23.49,23) rot=(0,0,-1;1.5708rad)
  TreeRank = 47
  _LinkOwner = 4607
  _LinkVersion = 1
FEATURE [App::Link] Link010  label="As3Traxxas5347ball"
  AutoLinkLabel = false
  AutoPlacement = true
  ElementCount = 2
  ElementList = -> [Link010_i0,Link010_i1]
  LinkedObject = -> Solid020
  SyncGroupVisibility = false
  TreeRank = 45
  _LinkOwner = 4486
  _LinkVersion = 1
FEATURE [Part::FeaturePython] Parts  # WARN: FeaturePython — macro-defined, semantics opaque (R4)
  Group = -> [Link,Link001,Link010]
  GroupMode = 0
  TreeRank = 0
  _LinkVersion = 1
FEATURE [Part::Feature] Solid020  label="5347 ball"
  TreeRank = 66
  shape: bbox 6.98 x 5.77 x 5.77 mm, 10 faces (baked)
FEATURE [Part::FeaturePython] Assembly  label="SubAs3kossel_carriage_MGN9C"  # WARN: FeaturePython — macro-defined, semantics opaque (R4)
  AutoRelax = true
  BuildShape = 0
  Freeze = true
  Group = -> [Constraints,Elements,Parts]
  TreeRank = 0
  Verbose = false
  _LinkVersion = 1
  _SolverType = 1
  _Version = 1
FEATURE [App::FeaturePython] Constraints  # WARN: FeaturePython — macro-defined, semantics opaque (R4)
  Group = -> [Constraint,Constraint001,Constraint003,Constraint004,Constraint005]
  TreeRank = 0
  _LinkVersion = 1
  _Version = 1
FEATURE [App::FeaturePython] Elements  # WARN: FeaturePython — macro-defined, semantics opaque (R4)
  Group = -> [_Element,_Element001,_Element003,_Element004,_Element005,Element,_Element006,_Element007,_Element008,_Element009,_Element010,_Element011,Element001,Element002]
  TreeRank = 0
  _LinkVersion = 1
FEATURE [App::FeaturePython] Constraint  label="Locked"  # WARN: FeaturePython — macro-defined, semantics opaque (R4)
  Disabled = false
  Group = -> [ElementLink]
  TreeRank = 0
  _ConstraintType = 0
  _LinkVersion = 1
  _Parent = -> Constraints
FEATURE [App::FeaturePython] ElementLink  label="Ref@As3MGN9CZFC-HiwinCorporation-3D-10-31-2021@"  # link proxy (typed FeaturePython)
  LinkTransform = true
  LinkedObject = -> _Element
  TreeRank = 0
  _LinkVersion = 1
  _Parent = -> Constraint
FEATURE [Part::FeaturePython] _Element  label="Ref@As3MGN9CZFC-HiwinCorporation-3D-10-31-2021@"  # link proxy (typed FeaturePython)
  Detach = false
  LinkTransform = true
  LinkedObject = -> Link [1.$Ref.]
  TreeRank = 0
  _LinkVersion = 1
  _Parent = -> Elements
FEATURE [Part::FeaturePython] _Element001  label="Fix1@As3MGN9CZFC-HiwinCorporation-3D-10-31-2021@"  # link proxy (typed FeaturePython)
  Detach = false
  LinkTransform = true
  LinkedObject = -> Link [1.$Fix1.]
  TreeRank = 0
  _LinkVersion = 1
  _Parent = -> Elements
FEATURE [Part::FeaturePython] _Element003  label="Fix2@As3MGN9CZFC-HiwinCorporation-3D-10-31-2021@"  # link proxy (typed FeaturePython)
  Detach = false
  LinkTransform = true
  LinkedObject = -> Link [1.$Fix2.]
  TreeRank = 0
  _LinkVersion = 1
  _Parent = -> Elements
FEATURE [App::FeaturePython] Constraint001  label="PlaneCoincident"  # WARN: FeaturePython — macro-defined, semantics opaque (R4)
  Angle = 0
  AnglePitch = 0
  AngleRoll = 0
  Cascade = false
  Disabled = false
  Group = -> [ElementLink001,ElementLink002]
  LockAngle = false
  Multiply = false
  OffsetX = 0
  OffsetY = 0
  TreeRank = 0
  _ConstraintType = 35
  _LinkVersion = 1
  _Parent = -> Constraints
FEATURE [App::FeaturePython] ElementLink001  label="Fix1@As3MGN9CZFC-HiwinCorporation-3D-10-31-2021@"  # link proxy (typed FeaturePython)
  LinkTransform = true
  LinkedObject = -> _Element001
  TreeRank = 0
  _LinkVersion = 1
  _Parent = -> Constraint001
FEATURE [App::FeaturePython] ElementLink002  label="Fix1@As3carriage_MGN9C@"  # link proxy (typed FeaturePython)
  LinkTransform = true
  LinkedObject = -> _Element004
  Offset = pos=(0,0,0) rot=(1,0,0;3.14159rad)
  Placement = pos=(38.9,-2.0572e-11,16) rot=(0,1,0;3.14159rad)
  TreeRank = 0
  _LinkVersion = 1
  _Parent = -> Constraint001
FEATURE [Part::FeaturePython] _Element004  label="Fix1@As3carriage_MGN9C@"  # link proxy (typed FeaturePython)
  Detach = false
  LinkTransform = true
  LinkedObject = -> Link001 [1.$Fix1.]
  TreeRank = 0
  _LinkVersion = 1
  _Parent = -> Elements
FEATURE [Part::FeaturePython] _Element005  label="Fix2@As3carriage_MGN9C@"  # link proxy (typed FeaturePython)
  Detach = false
  LinkTransform = true
  LinkedObject = -> Link001 [1.$Fix2.]
  TreeRank = 0
  _LinkVersion = 1
  _Parent = -> Elements
FEATURE [Part::FeaturePython] Element  label="Lat@As3MGN9CZFC-HiwinCorporation-3D-10-31-2021@"  # link proxy (typed FeaturePython)
  Detach = false
  LinkTransform = true
  LinkedObject = -> Link [1.$Lat.]
  TreeRank = 42
  _LinkVersion = 1
  _Parent = -> Elements
FEATURE [App::FeaturePython] Constraint003  label="SameOrientation"  # WARN: FeaturePython — macro-defined, semantics opaque (R4)
  Disabled = false
  Group = -> [ElementLink005,ElementLink006]
  TreeRank = 49
  _ConstraintType = 2
  _LinkVersion = 1
  _Parent = -> Constraints
FEATURE [App::FeaturePython] ElementLink005  label="_Element006"  # link proxy (typed FeaturePython)
  LinkTransform = true
  LinkedObject = -> _Element006
  TreeRank = 50
  _LinkVersion = 1
  _Parent = -> Constraint003
FEATURE [Part::FeaturePython] _Element006  # link proxy (typed FeaturePython)
  Detach = false
  LinkTransform = true
  LinkedObject = -> Link001 [1.$Element006.]
  TreeRank = 51
  _LinkVersion = 1
  _Parent = -> Elements
FEATURE [App::FeaturePython] ElementLink006  label="_Element007"  # link proxy (typed FeaturePython)
  LinkTransform = true
  LinkedObject = -> _Element007
  TreeRank = 52
  _LinkVersion = 1
  _Parent = -> Constraint003
FEATURE [Part::FeaturePython] _Element007  # link proxy (typed FeaturePython)
  Detach = false
  LinkTransform = true
  LinkedObject = -> Link [1.$Element004.]
  TreeRank = 53
  _LinkVersion = 1
  _Parent = -> Elements
FEATURE [App::FeaturePython] Constraint004  label="Attachment"  # WARN: FeaturePython — macro-defined, semantics opaque (R4)
  Cascade = false
  Disabled = false
  Group = -> [ElementLink007,ElementLink008]
  Multiply = false
  TreeRank = 54
  _ConstraintType = 45
  _LinkVersion = 1
  _Parent = -> Constraints
FEATURE [App::FeaturePython] ElementLink007  label="Rot1@As3carriage_MGN9C@"  # link proxy (typed FeaturePython)
  LinkTransform = true
  LinkedObject = -> _Element008
  TreeRank = 55
  _LinkVersion = 1
  _Parent = -> Constraint004
FEATURE [Part::FeaturePython] _Element008  label="Rot1@As3carriage_MGN9C@"  # link proxy (typed FeaturePython)
  Detach = false
  LinkTransform = true
  LinkedObject = -> Link001 [1.$Rot1.]
  TreeRank = 56
  _LinkVersion = 1
  _Parent = -> Elements
FEATURE [App::FeaturePython] ElementLink008  label="ElCircle@As3Traxxas5347ball@#0"  # link proxy (typed FeaturePython)
  LinkTransform = true
  LinkedObject = -> _Element009
  TreeRank = 57
  _LinkVersion = 1
  _Parent = -> Constraint004
FEATURE [Part::FeaturePython] _Element009  label="ElCircle@As3Traxxas5347ball@#0"  # link proxy (typed FeaturePython)
  Detach = false
  LinkTransform = true
  LinkedObject = -> Link010 [Link010_i0.Edge10]
  TreeRank = 58
  _LinkVersion = 1
  _Parent = -> Elements
FEATURE [App::FeaturePython] Constraint005  label="Attachment001"  # WARN: FeaturePython — macro-defined, semantics opaque (R4)
  Cascade = false
  Disabled = false
  Group = -> [ElementLink009,ElementLink010]
  Multiply = false
  TreeRank = 59
  _ConstraintType = 45
  _LinkVersion = 1
  _Parent = -> Constraints
FEATURE [App::FeaturePython] ElementLink009  label="Rot2@As3carriage_MGN9C@"  # link proxy (typed FeaturePython)
  LinkTransform = true
  LinkedObject = -> _Element010
  TreeRank = 60
  _LinkVersion = 1
  _Parent = -> Constraint005
FEATURE [Part::FeaturePython] _Element010  label="Rot2@As3carriage_MGN9C@"  # link proxy (typed FeaturePython)
  Detach = false
  LinkTransform = true
  LinkedObject = -> Link001 [1.$Rot2.]
  TreeRank = 61
  _LinkVersion = 1
  _Parent = -> Elements
FEATURE [App::FeaturePython] ElementLink010  label="ElCircle@As3Traxxas5347ball@#1"  # link proxy (typed FeaturePython)
  LinkTransform = true
  LinkedObject = -> _Element011
  TreeRank = 62
  _LinkVersion = 1
  _Parent = -> Constraint005
FEATURE [Part::FeaturePython] _Element011  label="ElCircle@As3Traxxas5347ball@#1"  # link proxy (typed FeaturePython)
  Detach = false
  LinkTransform = true
  LinkedObject = -> Link010 [Link010_i1.Edge10]
  TreeRank = 63
  _LinkVersion = 1
  _Parent = -> Elements
FEATURE [Part::FeaturePython] Element001  label="ElSphereM@As3Traxxas5347ball@#0"  # link proxy (typed FeaturePython)
  Detach = false
  LinkTransform = true
  LinkedObject = -> Link010 [Link010_i0.Face8]
  TreeRank = 64
  _LinkVersion = 1
  _Parent = -> Elements
FEATURE [Part::FeaturePython] Element002  label="ElSphereM@As3Traxxas5347ball@#1"  # link proxy (typed FeaturePython)
  Detach = false
  LinkTransform = true
  LinkedObject = -> Link010 [Link010_i1.Face8]
  TreeRank = 65
  _LinkVersion = 1
  _Parent = -> Elements
